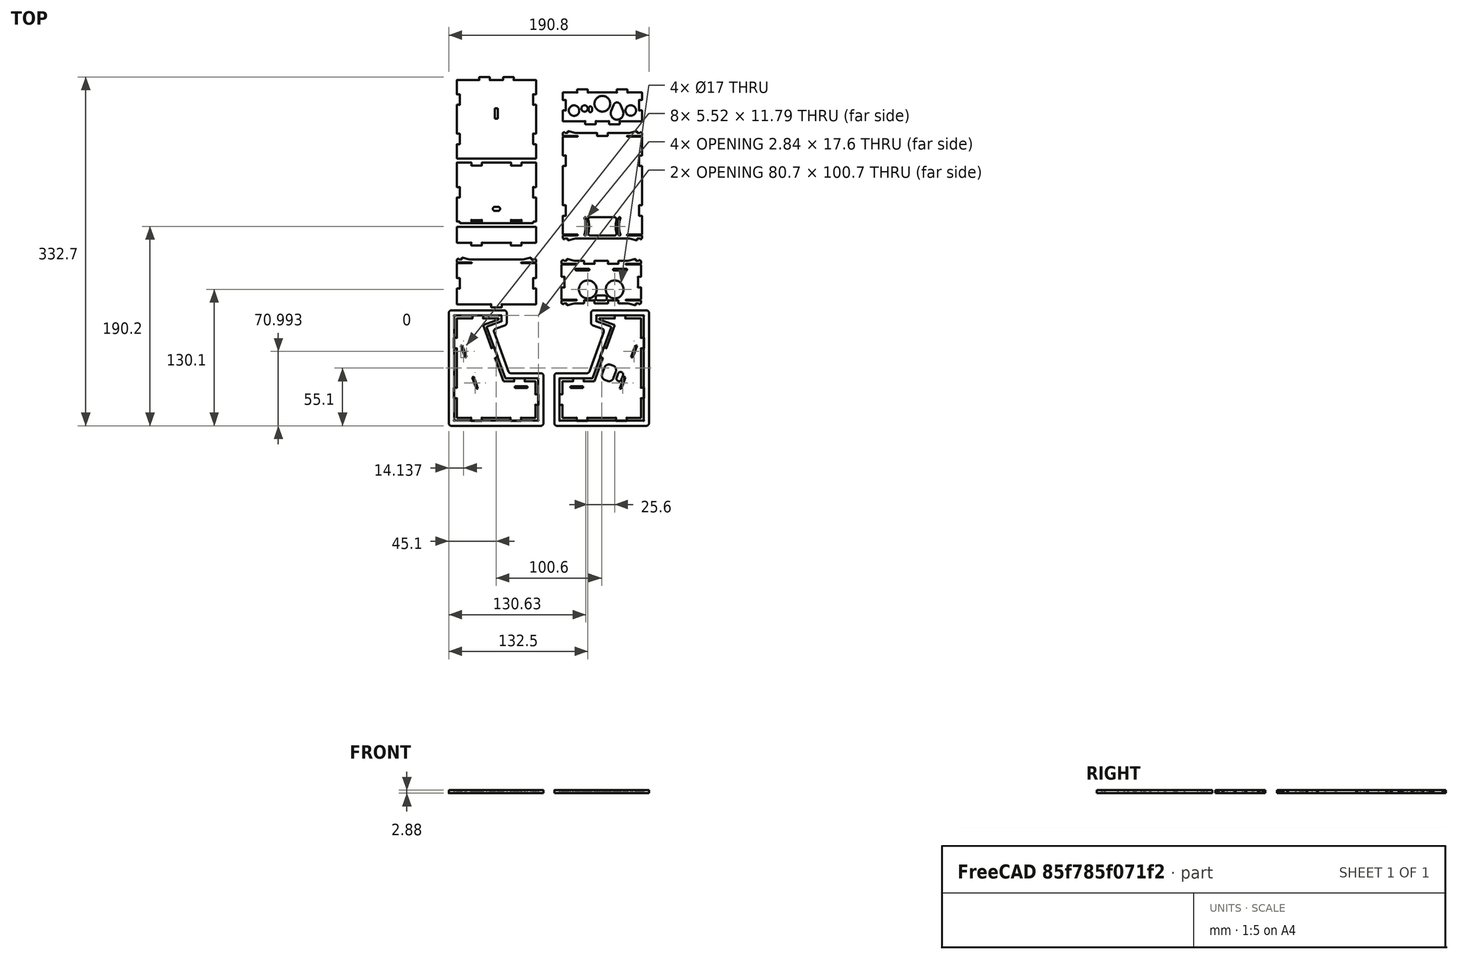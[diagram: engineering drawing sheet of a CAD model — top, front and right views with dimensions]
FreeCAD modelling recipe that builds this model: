
FCSTD DOCUMENT  (FreeCAD 1.0R39319 (Git))
Label: TheThing_v81_tabs_export
License: CERN Open Hardware Licence permissive
LicenseURL: https://cern-ohl.web.cern.ch/
objects: Part::Part2DObjectPython×13, Part::Feature×11, App::FeaturePython×11, Sketcher::SketchObject×10, Part::Chamfer×9, App::DocumentObjectGroup×4
note: 53 computed .brp shape members not serialized (recipe doc carries the construction recipe); baked Part::Feature solids carry a one-line shape summary decoded from their .brp

FEATURE [Part::Feature] test
  Placement = pos=(171.5,47,-35) rot=(-0.57735,-0.57735,-0.57735;2.0944rad)
  shape: bbox 80.6 x 100.6 x 2.8 mm, 82 faces (baked)
FEATURE [Part::Feature] test001
  Placement = pos=(30.5,47,-35) rot=(0.57735,-0.57735,-0.57735;4.18879rad)
  shape: bbox 80.6 x 100.6 x 2.8 mm, 70 faces (baked)
FEATURE [Part::Feature] test002
  Placement = pos=(152,221,20.1) rot=(-1,0,0;1.5708rad)
  shape: bbox 75.6 x 104.6 x 2.8 mm, 104 faces (baked)
FEATURE [Part::Feature] test003
  Placement = pos=(51,208,-25.7) rot=(-0.939693,0,0;1.22173rad)
  shape: bbox 75.6 x 58.11 x 2.925 mm, 56 faces (baked)
FEATURE [Part::Feature] test004
  Placement = pos=(152,353,-0.4) rot=(0,0,1;0rad)
  shape: bbox 75.6 x 33.14 x 2.8 mm, 54 faces (baked)
FEATURE [Part::Feature] test005
  Placement = pos=(150.9,159,60.5) rot=(0,0.707107,0.707107;3.14159rad)
  shape: bbox 75.6 x 44.6 x 2.8 mm, 108 faces (baked)
FEATURE [Part::Feature] test006
  Placement = pos=(51,277,-34.6) rot=(1,0,0;3.14159rad)
  shape: bbox 75.6 x 77.8 x 2.8 mm, 46 faces (baked)
FEATURE [Part::Feature] test007
  Placement = pos=(51,138,-60.4) rot=(0,0,1;3.14159rad)
  shape: bbox 75.6 x 47.6 x 2.8 mm, 50 faces (baked)
FEATURE [Part::Feature] test008
  Placement = pos=(51,151,48.1) rot=(-0.34202,0,0;2.79253rad)
  shape: bbox 75.6 x 17.92 x 2.8 mm, 18 faces (baked)
FEATURE [Part::Feature] test009
  Placement = pos=(171.5,47,-33) rot=(-0.57735,-0.57735,-0.57735;2.0944rad)
  shape: bbox 90.2 x 110.2 x 2.8 mm, 46 faces (baked)
FEATURE [Part::Feature] test010
  Placement = pos=(30.5,47,-33) rot=(0.57735,-0.57735,-0.57735;4.18879rad)
  shape: bbox 90.2 x 110.2 x 2.8 mm, 46 faces (baked)
FEATURE [Sketcher::SketchObject] Sketch
  ArcFitTolerance = 1e-06
  FullyConstrained = true
  MakeInternals = false
  sketch-geometry (52):
    g0: LineSegment StartX=5 StartY=0 StartZ=0 EndX=95 EndY=0 EndZ=0
    g1: LineSegment StartX=100 StartY=5 StartZ=0 EndX=100 EndY=165 EndZ=0
    g2: LineSegment StartX=95 StartY=170 StartZ=0 EndX=5 EndY=170 EndZ=0
    g3: LineSegment StartX=0 StartY=165 StartZ=0 EndX=0 EndY=5 EndZ=0
    g4: LineSegment StartX=5 StartY=171 StartZ=0 EndX=95 EndY=171 EndZ=0
    g5: LineSegment StartX=100 StartY=176 StartZ=0 EndX=100 EndY=336 EndZ=0
    g6: LineSegment StartX=95 StartY=341 StartZ=0 EndX=5 EndY=341 EndZ=0
    g7: LineSegment StartX=0 StartY=336 StartZ=0 EndX=0 EndY=176 EndZ=0
    g8: LineSegment StartX=106 StartY=171 StartZ=0 EndX=196 EndY=171 EndZ=0
    g9: LineSegment StartX=201 StartY=176 StartZ=0 EndX=201 EndY=336 EndZ=0
    g10: LineSegment StartX=196 StartY=341 StartZ=0 EndX=106 EndY=341 EndZ=0
    g11: LineSegment StartX=101 StartY=336 StartZ=0 EndX=101 EndY=176 EndZ=0
    g12: LineSegment StartX=106 StartY=0 StartZ=0 EndX=196 EndY=0 EndZ=0
    g13: LineSegment StartX=201 StartY=5 StartZ=0 EndX=201 EndY=165 EndZ=0
    g14: LineSegment StartX=196 StartY=170 StartZ=0 EndX=106 EndY=170 EndZ=0
    g15: LineSegment StartX=101 StartY=165 StartZ=0 EndX=101 EndY=5 EndZ=0
    g16: LineSegment [constr] StartX=100 StartY=170 StartZ=0 EndX=101 EndY=170 EndZ=0
    g17: LineSegment [constr] StartX=101 StartY=170 StartZ=0 EndX=101 EndY=171 EndZ=0
    g18: LineSegment [constr] StartX=101 StartY=171 StartZ=0 EndX=100 EndY=171 EndZ=0
    g19: LineSegment [constr] StartX=100 StartY=171 StartZ=0 EndX=100 EndY=170 EndZ=0
    g20: ArcOfCircle CenterX=5 CenterY=5 CenterZ=0 NormalX=0 NormalY=0 NormalZ=1 AngleXU=0 Radius=5 StartAngle=3.14159 EndAngle=4.71239
    g21: GeomPoint [constr] X=0 Y=0 Z=0
    g22: ArcOfCircle CenterX=95 CenterY=5 CenterZ=0 NormalX=0 NormalY=0 NormalZ=1 AngleXU=0 Radius=5 StartAngle=4.71239 EndAngle=6.28319
    g23: GeomPoint [constr] X=100 Y=0 Z=0
    g24: ArcOfCircle CenterX=106 CenterY=5 CenterZ=0 NormalX=0 NormalY=0 NormalZ=1 AngleXU=0 Radius=5 StartAngle=3.14159 EndAngle=4.71239
    g25: GeomPoint [constr] X=101 Y=0 Z=0
    g26: ArcOfCircle CenterX=196 CenterY=5 CenterZ=0 NormalX=0 NormalY=0 NormalZ=1 AngleXU=0 Radius=5 StartAngle=4.71239 EndAngle=6.28319
    g27: GeomPoint [constr] X=201 Y=0 Z=0
    g28: ArcOfCircle CenterX=95 CenterY=176 CenterZ=0 NormalX=0 NormalY=0 NormalZ=1 AngleXU=0 Radius=5 StartAngle=4.71239 EndAngle=6.28319
    g29: GeomPoint [constr] X=100 Y=171 Z=0
    g30: ArcOfCircle CenterX=95 CenterY=165 CenterZ=0 NormalX=0 NormalY=0 NormalZ=1 AngleXU=0 Radius=5 StartAngle=3e-16 EndAngle=1.5708
    g31: GeomPoint [constr] X=100 Y=170 Z=0
    g32: ArcOfCircle CenterX=106 CenterY=165 CenterZ=0 NormalX=0 NormalY=0 NormalZ=1 AngleXU=0 Radius=5 StartAngle=1.5708 EndAngle=3.14159
    g33: GeomPoint [constr] X=101 Y=170 Z=0
    g34: ArcOfCircle CenterX=106 CenterY=176 CenterZ=0 NormalX=0 NormalY=0 NormalZ=1 AngleXU=0 Radius=5 StartAngle=3.14159 EndAngle=4.71239
    g35: GeomPoint [constr] X=101 Y=171 Z=0
    g36: ArcOfCircle CenterX=5 CenterY=176 CenterZ=0 NormalX=0 NormalY=0 NormalZ=1 AngleXU=0 Radius=5 StartAngle=3.14159 EndAngle=4.71239
    g37: GeomPoint [constr] X=0 Y=171 Z=0
    g38: ArcOfCircle CenterX=196 CenterY=176 CenterZ=0 NormalX=0 NormalY=0 NormalZ=1 AngleXU=0 Radius=5 StartAngle=4.71239 EndAngle=6.28319
    g39: GeomPoint [constr] X=201 Y=171 Z=0
    g40: ArcOfCircle CenterX=196 CenterY=165 CenterZ=0 NormalX=0 NormalY=0 NormalZ=1 AngleXU=0 Radius=5 StartAngle=2.4e-15 EndAngle=1.5708
    g41: GeomPoint [constr] X=201 Y=170 Z=0
    g42: ArcOfCircle CenterX=5 CenterY=165 CenterZ=0 NormalX=0 NormalY=0 NormalZ=1 AngleXU=0 Radius=5 StartAngle=1.5708 EndAngle=3.14159
    g43: GeomPoint [constr] X=0 Y=170 Z=0
    g44: ArcOfCircle CenterX=5 CenterY=336 CenterZ=0 NormalX=0 NormalY=0 NormalZ=1 AngleXU=0 Radius=5 StartAngle=1.5708 EndAngle=3.14159
    g45: GeomPoint [constr] X=0 Y=341 Z=0
    g46: ArcOfCircle CenterX=95 CenterY=336 CenterZ=0 NormalX=0 NormalY=0 NormalZ=1 AngleXU=0 Radius=5 StartAngle=1.7e-15 EndAngle=1.5708
    g47: GeomPoint [constr] X=100 Y=341 Z=0
    g48: ArcOfCircle CenterX=106 CenterY=336 CenterZ=0 NormalX=0 NormalY=0 NormalZ=1 AngleXU=0 Radius=5 StartAngle=1.5708 EndAngle=3.14159
    g49: GeomPoint [constr] X=101 Y=341 Z=0
    g50: ArcOfCircle CenterX=196 CenterY=336 CenterZ=0 NormalX=0 NormalY=0 NormalZ=1 AngleXU=0 Radius=5 StartAngle=-2.7e-15 EndAngle=1.5708
    g51: GeomPoint [constr] X=201 Y=341 Z=0
  constraints (119):
    c: Horizontal(g0)
    c: Horizontal(g2)
    c: Vertical(g1)
    c: Vertical(g3)
    c: Coincident(g21,g-1)
    c: Horizontal(g4)
    c: Horizontal(g6)
    c: Vertical(g5)
    c: Vertical(g7)
    c: Horizontal(g8)
    c: Horizontal(g10)
    c: Vertical(g9)
    c: Vertical(g11)
    c: Horizontal(g12)
    c: Horizontal(g14)
    c: Vertical(g13)
    c: Vertical(g15)
    c: DistanceX(g21,g23) = 100
    c: DistanceY(g21,g43) = 170
    c: Coincident(g16,g17)
    c: Coincident(g17,g18)
    c: Coincident(g18,g19)
    c: Coincident(g19,g16)
    c: Horizontal(g16)
    c: Horizontal(g18)
    c: Vertical(g17)
    c: Vertical(g19)
    c: Distance(g17,g19) = 1
    c: Distance(g16,g18) = 1
    c: Coincident(g16,g31)
    c: Coincident(g18,g29)
    c: Coincident(g17,g35)
    c: Coincident(g16,g33)
    c: PointOnObject(g21,g0)
    c: PointOnObject(g21,g3)
    c: Tangent(g0,g20) = -1.5708
    c: Tangent(g3,g20) = -1.5708
    c: PointOnObject(g23,g0)
    c: PointOnObject(g23,g1)
    c: Tangent(g0,g22) = -1.5708
    c: Tangent(g1,g22) = -1.5708
    c: PointOnObject(g25,g12)
    c: PointOnObject(g25,g15)
    c: Tangent(g12,g24) = -1.5708
    c: Tangent(g15,g24) = -1.5708
    c: PointOnObject(g27,g13)
    c: PointOnObject(g27,g12)
    c: Tangent(g13,g26) = -1.5708
    c: Tangent(g12,g26) = -1.5708
    c: PointOnObject(g29,g5)
    c: PointOnObject(g29,g4)
    c: Tangent(g5,g28) = -1.5708
    c: Tangent(g4,g28) = -1.5708
    c: PointOnObject(g31,g2)
    c: PointOnObject(g31,g1)
    c: Tangent(g2,g30) = -1.5708
    c: Tangent(g1,g30) = -1.5708
    c: PointOnObject(g33,g14)
    c: PointOnObject(g33,g15)
    c: Tangent(g14,g32) = -1.5708
    c: Tangent(g15,g32) = -1.5708
    c: PointOnObject(g35,g8)
    c: PointOnObject(g35,g11)
    c: Tangent(g8,g34) = -1.5708
    c: Tangent(g11,g34) = -1.5708
    c: PointOnObject(g37,g4)
    c: PointOnObject(g37,g7)
    c: Tangent(g4,g36) = -1.5708
    c: Tangent(g7,g36) = -1.5708
    c: PointOnObject(g39,g8)
    c: PointOnObject(g39,g9)
    c: Tangent(g8,g38) = -1.5708
    c: Tangent(g9,g38) = -1.5708
    c: PointOnObject(g41,g14)
    c: PointOnObject(g41,g13)
    c: Tangent(g14,g40) = -1.5708
    c: Tangent(g13,g40) = -1.5708
    c: PointOnObject(g43,g2)
    c: PointOnObject(g43,g3)
    c: Tangent(g2,g42) = -1.5708
    c: Tangent(g3,g42) = -1.5708
    c: PointOnObject(g45,g6)
    c: PointOnObject(g45,g7)
    c: Tangent(g6,g44) = -1.5708
    c: Tangent(g7,g44) = -1.5708
    c: PointOnObject(g47,g6)
    c: PointOnObject(g47,g5)
    c: Tangent(g6,g46) = -1.5708
    c: Tangent(g5,g46) = -1.5708
    c: PointOnObject(g49,g10)
    c: PointOnObject(g49,g11)
    c: Tangent(g10,g48) = -1.5708
    c: Tangent(g11,g48) = -1.5708
    c: PointOnObject(g51,g10)
    c: PointOnObject(g51,g9)
    c: Tangent(g10,g50) = -1.5708
    c: Tangent(g9,g50) = -1.5708
    c: Equal(g50,g48)
    c: Equal(g48,g46)
    c: Equal(g46,g44)
    c: Equal(g44,g36)
    c: Equal(g36,g42)
    c: Equal(g42,g28)
    c: Equal(g28,g34)
    c: Equal(g34,g32)
    c: Equal(g32,g30)
    c: Equal(g30,g38)
    c: Equal(g38,g40)
    c: Equal(g40,g26)
    c: Equal(g26,g24)
    c: Equal(g24,g22)
    c: Equal(g22,g20)
    c: Radius(g20) = 5
    c: Vertical(g37,g43)
    c: Horizontal(g25,g23)
    c: Vertical(g39,g41)
    c: Horizontal(g47,g49)
    c: Equal(g7,g3)
    c: Equal(g6,g10)
FEATURE [Part::Chamfer] Chamfer
  Base = -> test
  EdgeLinks = -> test [Edge25,Edge27,Edge39,Edge50,Edge52,Edge72,Edge74,Edge86,Edge97,Edge99,Edge119,Edge121,Edge133,Edge144,Edge146,Edge158,Edge169,Edge171,Edge194,Edge196]
  Edges = 20 edges r=0.5: [Edge25,Edge27,Edge39,Edge50,Edge52,Edge72,Edge74,Edge86,Edge97,Edge99,Edge119,Edge121,Edge133,Edge144,Edge146,Edge158,Edge169,Edge171,Edge194,Edge196]
FEATURE [Part::Chamfer] Chamfer001
  Base = -> test001
  EdgeLinks = -> test001 [Edge25,Edge27,Edge39,Edge50,Edge52,Edge72,Edge74,Edge86,Edge97,Edge99,Edge119,Edge121,Edge133,Edge144,Edge146,Edge158,Edge169,Edge171,Edge194,Edge196]
  Edges = 20 edges r=0.5: [Edge25,Edge27,Edge39,Edge50,Edge52,Edge72,Edge74,Edge86,Edge97,Edge99,Edge119,Edge121,Edge133,Edge144,Edge146,Edge158,Edge169,Edge171,Edge194,Edge196]
FEATURE [Part::Chamfer] Chamfer002
  Base = -> test002
  EdgeLinks = -> test002 [Edge227,Edge232,Edge233,Edge238,Edge267,Edge272,Edge273,Edge278,Edge293,Edge298]
  Edges = 10 edges r=0.5: [Edge227,Edge232,Edge233,Edge238,Edge267,Edge272,Edge273,Edge278,Edge293,Edge298]
FEATURE [Part::Chamfer] Chamfer003
  Base = -> test003
  EdgeLinks = -> test003 [Edge2,Edge4,Edge104,Edge105,Edge107,Edge118,Edge142,Edge143,Edge148,Edge149,Edge150,Edge155,Edge156,Edge164]
  Edges = 14 edges r=0.5: [Edge2,Edge4,Edge104,Edge105,Edge107,Edge118,Edge142,Edge143,Edge148,Edge149,Edge150,Edge155,Edge156,Edge164]
FEATURE [Part::Chamfer] Chamfer004
  Base = -> test004
  EdgeLinks = -> test004 [Edge4,Edge7,Edge17,Edge20,Edge39,Edge42,Edge52,Edge55,Edge69,Edge73,Edge85,Edge88,Edge107,Edge110,Edge115,Edge123]
  Edges = 16 edges: [Edge4 r=0.5,Edge7 r=1,Edge17 r=0.5,Edge20 r=0.5,Edge39 r=0.5,Edge42 r=0.5,Edge52 r=0.5,Edge55 r=0.5,Edge69 r=0.5,Edge73 r=0.5,Edge85 r=0.5,Edge88 r=0.5,Edge107 r=0.5,Edge110 r=0.5,Edge115 r=0.5,Edge123 r=0.5]
FEATURE [Part::Chamfer] Chamfer005
  Base = -> test005
  EdgeLinks = -> test005 [Edge243,Edge248,Edge249,Edge254,Edge269,Edge274,Edge289,Edge294,Edge295,Edge300,Edge315,Edge320]
  Edges = 12 edges r=0.5: [Edge243,Edge248,Edge249,Edge254,Edge269,Edge274,Edge289,Edge294,Edge295,Edge300,Edge315,Edge320]
FEATURE [Part::Chamfer] Chamfer006
  Base = -> test006
  EdgeLinks = -> test006 [Edge1,Edge2,Edge7,Edge9,Edge27,Edge30,Edge45,Edge48,Edge59,Edge61,Edge81,Edge83,Edge95,Edge98,Edge125,Edge126]
  Edges = 16 edges r=0.5: [Edge1,Edge2,Edge7,Edge9,Edge27,Edge30,Edge45,Edge48,Edge59,Edge61,Edge81,Edge83,Edge95,Edge98,Edge125,Edge126]
FEATURE [Part::Chamfer] Chamfer007
  Base = -> test007
  EdgeLinks = -> test007 [Edge4,Edge6,Edge17,Edge20,Edge87,Edge103,Edge106,Edge120]
  Edges = 8 edges r=0.5: [Edge4,Edge6,Edge17,Edge20,Edge87,Edge103,Edge106,Edge120]
FEATURE [Part::Chamfer] Chamfer008
  Base = -> test008
  EdgeLinks = -> test008 [Edge1,Edge2,Edge5,Edge8,Edge28,Edge31,Edge50,Edge53]
  Edges = 8 edges r=0.5: [Edge1,Edge2,Edge5,Edge8,Edge28,Edge31,Edge50,Edge53]
FEATURE [Part::Part2DObjectPython] Shape2DView  # Draft 2D object (typed FeaturePython)
  AutoUpdate = true
  Clip = false
  FuseArch = false
  HiddenLines = false
  InPlace = true
  OnlySolids = false
  Placement = pos=(92,350,3) rot=(0,0,1;1.5708rad)
  Projection = (-0.0061258,0.0189136,0.999802)
  ProjectionMode = 0
  SegmentLength = 0.05
  Tessellation = false
  VisibleOnly = false
FEATURE [Part::Part2DObjectPython] Shape2DView001  # Draft 2D object (typed FeaturePython)
  AutoUpdate = true
  Clip = false
  FuseArch = false
  HiddenLines = false
  InPlace = true
  OnlySolids = false
  Placement = pos=(138,9,3) rot=(0,0,1;3.14159rad)
  Projection = (0,0,1)
  ProjectionMode = 0
  SegmentLength = 0.05
  Tessellation = false
  VisibleOnly = false
FEATURE [App::FeaturePython] Text  # WARN: FeaturePython — macro-defined, semantics opaque (R4)
  Placement = pos=(167,104,0) rot=(0,0,1;0rad)
  Text = [1]
FEATURE [App::FeaturePython] Text001  # WARN: FeaturePython — macro-defined, semantics opaque (R4)
  Placement = pos=(31,104,0) rot=(0,0,1;0rad)
  Text = [2]
FEATURE [App::FeaturePython] Text002  # WARN: FeaturePython — macro-defined, semantics opaque (R4)
  Placement = pos=(150,277,0) rot=(0,0,1;0rad)
  Text = [3]
FEATURE [App::FeaturePython] Text003  # WARN: FeaturePython — macro-defined, semantics opaque (R4)
  Placement = pos=(49,249,0) rot=(0,0,1;0rad)
  Text = [4]
FEATURE [App::FeaturePython] Text004  # WARN: FeaturePython — macro-defined, semantics opaque (R4)
  Placement = pos=(150,320,0) rot=(0,0,1;0rad)
  Text = [5]
FEATURE [App::FeaturePython] Text005  # WARN: FeaturePython — macro-defined, semantics opaque (R4)
  Placement = pos=(149,156,0) rot=(0,0,1;0rad)
  Text = [6]
FEATURE [App::FeaturePython] Text006  # WARN: FeaturePython — macro-defined, semantics opaque (R4)
  Placement = pos=(49,331,0) rot=(0,0,1;0rad)
  Text = [7]
FEATURE [App::FeaturePython] Text007  # WARN: FeaturePython — macro-defined, semantics opaque (R4)
  Placement = pos=(48,160,0) rot=(0,0,1;0rad)
  Text = [8]
FEATURE [App::FeaturePython] Text008  # WARN: FeaturePython — macro-defined, semantics opaque (R4)
  Placement = pos=(49,191,0) rot=(0,0,1;0rad)
  Text = [9]
FEATURE [App::FeaturePython] Text009  # WARN: FeaturePython — macro-defined, semantics opaque (R4)
  Placement = pos=(166,111.5,0) rot=(0,0,1;0rad)
  Text = [10]
FEATURE [App::FeaturePython] Text010  # WARN: FeaturePython — macro-defined, semantics opaque (R4)
  Placement = pos=(30,111.5,0) rot=(0,0,1;0rad)
  Text = [11]
FEATURE [App::DocumentObjectGroup] Group  label="Numbers"
  Group = -> [Text,Text001,Text002,Text003,Text004,Text005,Text006,Text007,Text008,Text009,Text010]
FEATURE [App::DocumentObjectGroup] Group001  label="Logos"
  Group = -> [Shape2DView,Shape2DView001]
FEATURE [Part::Part2DObjectPython] Shape2DView002  # Draft 2D object (typed FeaturePython)
  AutoUpdate = true
  Base = -> test009
  Clip = false
  FuseArch = false
  HiddenLines = false
  InPlace = true
  OnlySolids = false
  Projection = (0,0,1)
  ProjectionMode = 0
  SegmentLength = 0.05
  Tessellation = false
  VisibleOnly = false
FEATURE [Part::Part2DObjectPython] Shape2DView003  # Draft 2D object (typed FeaturePython)
  AutoUpdate = true
  Base = -> Chamfer
  Clip = false
  FuseArch = false
  HiddenLines = false
  InPlace = true
  OnlySolids = false
  Projection = (0,0,1)
  ProjectionMode = 0
  SegmentLength = 0.05
  Tessellation = false
  VisibleOnly = false
FEATURE [Part::Part2DObjectPython] Shape2DView004  # Draft 2D object (typed FeaturePython)
  AutoUpdate = true
  Base = -> test010
  Clip = false
  FuseArch = false
  HiddenLines = false
  InPlace = true
  OnlySolids = false
  Projection = (0,0,1)
  ProjectionMode = 0
  SegmentLength = 0.05
  Tessellation = false
  VisibleOnly = false
FEATURE [Part::Part2DObjectPython] Shape2DView005  # Draft 2D object (typed FeaturePython)
  AutoUpdate = true
  Base = -> Chamfer001
  Clip = false
  FuseArch = false
  HiddenLines = false
  InPlace = true
  OnlySolids = false
  Projection = (0,0,1)
  ProjectionMode = 0
  SegmentLength = 0.05
  Tessellation = false
  VisibleOnly = false
FEATURE [Part::Part2DObjectPython] Shape2DView006  # Draft 2D object (typed FeaturePython)
  AutoUpdate = true
  Base = -> Chamfer002
  Clip = false
  FuseArch = false
  HiddenLines = false
  InPlace = true
  OnlySolids = false
  Projection = (0,0,1)
  ProjectionMode = 0
  SegmentLength = 0.05
  Tessellation = false
  VisibleOnly = false
FEATURE [Part::Part2DObjectPython] Shape2DView007  # Draft 2D object (typed FeaturePython)
  AutoUpdate = true
  Base = -> Chamfer003
  Clip = false
  FuseArch = false
  HiddenLines = false
  InPlace = true
  OnlySolids = false
  Projection = (0,0,1)
  ProjectionMode = 0
  SegmentLength = 0.05
  Tessellation = false
  VisibleOnly = false
FEATURE [Part::Part2DObjectPython] Shape2DView008  # Draft 2D object (typed FeaturePython)
  AutoUpdate = true
  Base = -> Chamfer004
  Clip = false
  FuseArch = false
  HiddenLines = false
  InPlace = true
  OnlySolids = false
  Projection = (0,0,1)
  ProjectionMode = 0
  SegmentLength = 0.05
  Tessellation = false
  VisibleOnly = false
FEATURE [Part::Part2DObjectPython] Shape2DView009  # Draft 2D object (typed FeaturePython)
  AutoUpdate = true
  Base = -> Chamfer005
  Clip = false
  FuseArch = false
  HiddenLines = false
  InPlace = true
  OnlySolids = false
  Projection = (0,0,1)
  ProjectionMode = 0
  SegmentLength = 0.05
  Tessellation = false
  VisibleOnly = false
FEATURE [Part::Part2DObjectPython] Shape2DView010  # Draft 2D object (typed FeaturePython)
  AutoUpdate = true
  Base = -> Chamfer006
  Clip = false
  FuseArch = false
  HiddenLines = false
  InPlace = true
  OnlySolids = false
  Projection = (0,0,1)
  ProjectionMode = 0
  SegmentLength = 0.05
  Tessellation = false
  VisibleOnly = false
FEATURE [Part::Part2DObjectPython] Shape2DView011  # Draft 2D object (typed FeaturePython)
  AutoUpdate = true
  Base = -> Chamfer007
  Clip = false
  FuseArch = false
  HiddenLines = false
  InPlace = true
  OnlySolids = false
  Projection = (0,0,1)
  ProjectionMode = 0
  SegmentLength = 0.05
  Tessellation = false
  VisibleOnly = false
FEATURE [Part::Part2DObjectPython] Shape2DView012  # Draft 2D object (typed FeaturePython)
  AutoUpdate = true
  Base = -> Chamfer008
  Clip = false
  FuseArch = false
  HiddenLines = false
  InPlace = true
  OnlySolids = false
  Projection = (0,0,1)
  ProjectionMode = 0
  SegmentLength = 0.05
  Tessellation = false
  VisibleOnly = false
FEATURE [Sketcher::SketchObject] Sketch001
  ArcFitTolerance = 1e-06
  FullyConstrained = false
  MakeInternals = false
  sketch-geometry (152):
    g0: LineSegment StartX=143.7 StartY=115 StartZ=0 EndX=193.9 EndY=115 EndZ=0
    g1: ArcOfCircle CenterX=143.7 CenterY=112.5 CenterZ=0 NormalX=0 NormalY=0 NormalZ=1 AngleXU=1.8e-15 Radius=2.5 StartAngle=1.5708 EndAngle=3.14159
    g2: ArcOfCircle CenterX=193.9 CenterY=112.5 CenterZ=0 NormalX=0 NormalY=0 NormalZ=1 AngleXU=1.8e-15 Radius=2.5 StartAngle=0 EndAngle=1.5708
    g3: LineSegment StartX=141.2 StartY=103.131 StartZ=0 EndX=141.2 EndY=112.5 EndZ=0
    g4: LineSegment StartX=196.4 StartY=112.5 StartZ=0 EndX=196.4 EndY=7.3 EndZ=0
    g5: ArcOfCircle CenterX=143.7 CenterY=103.131 CenterZ=0 NormalX=0 NormalY=0 NormalZ=1 AngleXU=1.8e-15 Radius=2.5 StartAngle=3.14159 EndAngle=4.36332
    g6: ArcOfCircle CenterX=193.9 CenterY=7.3 CenterZ=0 NormalX=0 NormalY=0 NormalZ=1 AngleXU=1.8e-15 Radius=2.5 StartAngle=4.71239 EndAngle=6.28319
    g7: LineSegment StartX=151.813 StartY=97.5174 StartZ=0 EndX=142.845 EndY=100.781 EndZ=0
    g8: LineSegment StartX=193.9 StartY=4.8 StartZ=0 EndX=108.7 EndY=4.8 EndZ=0
    g9: ArcOfCircle CenterX=150.958 CenterY=95.1682 CenterZ=0 NormalX=0 NormalY=0 NormalZ=1 AngleXU=1.8e-15 Radius=2.5 StartAngle=5.93412 EndAngle=7.50492
    g10: ArcOfCircle CenterX=108.7 CenterY=7.3 CenterZ=0 NormalX=0 NormalY=0 NormalZ=1 AngleXU=1.8e-15 Radius=2.5 StartAngle=3.14159 EndAngle=4.71239
    g11: LineSegment StartX=139.597 StartY=56.6449 StartZ=0 EndX=153.307 EndY=94.3131 EndZ=0
    g12: LineSegment StartX=106.2 StartY=7.3 StartZ=0 EndX=106.2 EndY=52.5 EndZ=0
    g13: ArcOfCircle CenterX=137.248 CenterY=57.5 CenterZ=0 NormalX=0 NormalY=0 NormalZ=1 AngleXU=1.8e-15 Radius=2.5 StartAngle=4.71239 EndAngle=5.93412
    g14: ArcOfCircle CenterX=108.7 CenterY=52.5 CenterZ=0 NormalX=0 NormalY=0 NormalZ=1 AngleXU=1.8e-15 Radius=2.5 StartAngle=1.5708 EndAngle=3.14159
    g15: LineSegment StartX=108.7 StartY=55 StartZ=0 EndX=137.248 EndY=55 EndZ=0
    g16: ArcOfCircle CenterX=146.633 CenterY=110.25 CenterZ=0 NormalX=0 NormalY=0 NormalZ=1 AngleXU=1.7e-15 Radius=0.25 StartAngle=3.66519 EndAngle=4.71239
    g17: ArcOfCircle CenterX=146.2 CenterY=110 CenterZ=0 NormalX=0 NormalY=0 NormalZ=1 AngleXU=1.7e-15 Radius=0.25 StartAngle=0.523599 EndAngle=4.18879
    g18: ArcOfCircle CenterX=145.95 CenterY=109.567 CenterZ=0 NormalX=0 NormalY=0 NormalZ=1 AngleXU=1.7e-15 Radius=0.25 StartAngle=-8.9e-15 EndAngle=1.0472
    g19: LineSegment StartX=146.2 StartY=104.993 StartZ=0 EndX=146.2 EndY=109.567 EndZ=0
    g20: ArcOfCircle CenterX=145.95 CenterY=104.993 CenterZ=0 NormalX=0 NormalY=0 NormalZ=1 AngleXU=1.7e-15 Radius=0.25 StartAngle=5.23599 EndAngle=6.28319
    g21: ArcOfCircle CenterX=146.2 CenterY=104.56 CenterZ=0 NormalX=0 NormalY=0 NormalZ=1 AngleXU=1.7e-15 Radius=0.25 StartAngle=2.0944 EndAngle=5.41052
    g22: ArcOfCircle CenterX=146.521 CenterY=104.177 CenterZ=0 NormalX=0 NormalY=0 NormalZ=1 AngleXU=1.7e-15 Radius=0.25 StartAngle=1.22173 EndAngle=2.26893
    g23: LineSegment StartX=159.528 StartY=99.7094 StartZ=0 EndX=146.607 EndY=104.412 EndZ=0
    g24: ArcOfCircle CenterX=159.186 CenterY=98.7697 CenterZ=0 NormalX=0 NormalY=0 NormalZ=1 AngleXU=1.8e-15 Radius=1 StartAngle=5.93412 EndAngle=7.50492
    g25: LineSegment StartX=142.739 StartY=50.658 StartZ=0 EndX=160.126 EndY=98.4277 EndZ=0
    g26: ArcOfCircle CenterX=141.799 CenterY=51 CenterZ=0 NormalX=0 NormalY=0 NormalZ=1 AngleXU=1.8e-15 Radius=1 StartAngle=4.71239 EndAngle=5.93412
    g27: LineSegment StartX=111.633 StartY=50 StartZ=0 EndX=141.799 EndY=50 EndZ=0
    g28: ArcOfCircle CenterX=111.633 CenterY=50.25 CenterZ=0 NormalX=0 NormalY=0 NormalZ=1 AngleXU=1.7e-15 Radius=0.25 StartAngle=3.66519 EndAngle=4.71239
    g29: ArcOfCircle CenterX=111.2 CenterY=50 CenterZ=0 NormalX=0 NormalY=0 NormalZ=1 AngleXU=1.7e-15 Radius=0.25 StartAngle=0.523599 EndAngle=4.18879
    g30: ArcOfCircle CenterX=110.95 CenterY=49.567 CenterZ=0 NormalX=0 NormalY=0 NormalZ=1 AngleXU=1.7e-15 Radius=0.25 StartAngle=1e-15 EndAngle=1.0472
    g31: LineSegment StartX=111.2 StartY=10.233 StartZ=0 EndX=111.2 EndY=49.567 EndZ=0
    g32: ArcOfCircle CenterX=110.95 CenterY=10.233 CenterZ=0 NormalX=0 NormalY=0 NormalZ=1 AngleXU=1.7e-15 Radius=0.25 StartAngle=5.23599 EndAngle=6.28319
    g33: ArcOfCircle CenterX=111.2 CenterY=9.8 CenterZ=0 NormalX=0 NormalY=0 NormalZ=1 AngleXU=1.7e-15 Radius=0.25 StartAngle=2.0944 EndAngle=5.75959
    g34: ArcOfCircle CenterX=111.633 CenterY=9.55 CenterZ=0 NormalX=0 NormalY=0 NormalZ=1 AngleXU=1.7e-15 Radius=0.25 StartAngle=1.5708 EndAngle=2.61799
    g35: LineSegment StartX=190.967 StartY=9.8 StartZ=0 EndX=111.633 EndY=9.8 EndZ=0
    g36: ArcOfCircle CenterX=190.967 CenterY=9.55 CenterZ=0 NormalX=0 NormalY=0 NormalZ=1 AngleXU=1.7e-15 Radius=0.25 StartAngle=0.523599 EndAngle=1.5708
    g37: ArcOfCircle CenterX=191.4 CenterY=9.8 CenterZ=0 NormalX=0 NormalY=0 NormalZ=1 AngleXU=1.7e-15 Radius=0.25 StartAngle=3.66519 EndAngle=7.33038
    g38: ArcOfCircle CenterX=191.65 CenterY=10.233 CenterZ=0 NormalX=0 NormalY=0 NormalZ=1 AngleXU=1.7e-15 Radius=0.25 StartAngle=3.14159 EndAngle=4.18879
    g39: LineSegment StartX=191.4 StartY=109.567 StartZ=0 EndX=191.4 EndY=10.233 EndZ=0
    g40: ArcOfCircle CenterX=191.65 CenterY=109.567 CenterZ=0 NormalX=0 NormalY=0 NormalZ=1 AngleXU=1.7e-15 Radius=0.25 StartAngle=2.0944 EndAngle=3.14159
    g41: ArcOfCircle CenterX=191.4 CenterY=110 CenterZ=0 NormalX=0 NormalY=0 NormalZ=1 AngleXU=1.7e-15 Radius=0.25 StartAngle=5.23599 EndAngle=8.90118
    g42: ArcOfCircle CenterX=190.967 CenterY=110.25 CenterZ=0 NormalX=0 NormalY=0 NormalZ=1 AngleXU=1.7e-15 Radius=0.25 StartAngle=4.71239 EndAngle=5.75959
    g43: LineSegment StartX=146.633 StartY=110 StartZ=0 EndX=190.967 EndY=110 EndZ=0
    g44: LineSegment StartX=163.725 StartY=107.587 StartZ=0 EndX=163.725 EndY=109.7 EndZ=0
    g45: LineSegment StartX=163.725 StartY=109.7 StartZ=0 EndX=164.025 EndY=110 EndZ=0
    g46: ArcOfCircle CenterX=163.725 CenterY=107.4 CenterZ=0 NormalX=0 NormalY=0 NormalZ=1 AngleXU=1.5708 Radius=0.186667 StartAngle=1.5708 EndAngle=4.71239
    g47: ArcOfCircle CenterX=163.725 CenterY=107.4 CenterZ=0 NormalX=0 NormalY=0 NormalZ=1 AngleXU=1.5708 Radius=0.186667 StartAngle=4.71239 EndAngle=6.28319
    g48: LineSegment StartX=155.62 StartY=78.9934 StartZ=0 EndX=153.634 EndY=79.7163 EndZ=0
    g49: LineSegment StartX=153.25 StartY=79.5369 StartZ=0 EndX=153.634 EndY=79.7163 EndZ=0
    g50: ArcOfCircle CenterX=155.796 CenterY=78.9296 CenterZ=0 NormalX=0 NormalY=0 NormalZ=1 AngleXU=2.79253 Radius=0.186667 StartAngle=0 EndAngle=1.5708
    g51: ArcOfCircle CenterX=155.796 CenterY=78.9296 CenterZ=0 NormalX=0 NormalY=0 NormalZ=1 AngleXU=2.79253 Radius=0.186667 StartAngle=1.5708 EndAngle=4.71239
    g52: LineSegment StartX=150.163 StartY=70.1784 StartZ=0 EndX=149.984 EndY=70.5629 EndZ=0
    g53: LineSegment StartX=155.86 StartY=79.105 StartZ=0 EndX=163.8 EndY=100.921 EndZ=0
    g54: LineSegment StartX=152.149 StartY=69.4556 StartZ=0 EndX=150.163 EndY=70.1784 EndZ=0
    g55: LineSegment StartX=163.8 StartY=100.921 StartZ=0 EndX=148.8 EndY=106.381 EndZ=0
    g56: ArcOfCircle CenterX=152.324 CenterY=69.3917 CenterZ=0 NormalX=0 NormalY=0 NormalZ=1 AngleXU=2.79253 Radius=0.186667 StartAngle=4.71239 EndAngle=6.28319
    g57: LineSegment StartX=148.8 StartY=106.381 StartZ=0 EndX=148.8 EndY=107.4 EndZ=0
    g58: ArcOfCircle CenterX=152.324 CenterY=69.3917 CenterZ=0 NormalX=0 NormalY=0 NormalZ=1 AngleXU=2.79253 Radius=0.186667 StartAngle=1.5708 EndAngle=4.71239
    g59: LineSegment StartX=148.8 StartY=107.4 StartZ=0 EndX=163.538 EndY=107.4 EndZ=0
    g60: LineSegment StartX=144.32 StartY=47.4 StartZ=0 EndX=152.26 EndY=69.2163 EndZ=0
    g61: LineSegment StartX=134.322 StartY=47.4 StartZ=0 EndX=144.32 EndY=47.4 EndZ=0
    g62: ArcOfCircle CenterX=134.135 CenterY=47.4 CenterZ=0 NormalX=0 NormalY=0 NormalZ=1 AngleXU=1.5708 Radius=0.186667 StartAngle=1.5708 EndAngle=4.71239
    g63: ArcOfCircle CenterX=134.135 CenterY=47.4 CenterZ=0 NormalX=0 NormalY=0 NormalZ=1 AngleXU=1.5708 Radius=0.186667 StartAngle=0 EndAngle=1.5708
    g64: LineSegment StartX=134.135 StartY=47.5867 StartZ=0 EndX=134.135 EndY=49.7 EndZ=0
    g65: LineSegment StartX=133.835 StartY=50 StartZ=0 EndX=134.135 EndY=49.7 EndZ=0
    g66: LineSegment StartX=173.575 StartY=110 StartZ=0 EndX=173.875 EndY=109.7 EndZ=0
    g67: LineSegment StartX=173.875 StartY=107.587 StartZ=0 EndX=173.875 EndY=109.7 EndZ=0
    g68: LineSegment StartX=123.985 StartY=49.7 StartZ=0 EndX=124.285 EndY=50 EndZ=0
    g69: ArcOfCircle CenterX=173.875 CenterY=107.4 CenterZ=0 NormalX=0 NormalY=0 NormalZ=1 AngleXU=1.5708 Radius=0.186667 StartAngle=0 EndAngle=1.5708
    g70: LineSegment StartX=123.985 StartY=47.5867 StartZ=0 EndX=123.985 EndY=49.7 EndZ=0
    g71: ArcOfCircle CenterX=173.875 CenterY=107.4 CenterZ=0 NormalX=0 NormalY=0 NormalZ=1 AngleXU=1.5708 Radius=0.186667 StartAngle=1.5708 EndAngle=4.71239
    g72: ArcOfCircle CenterX=123.985 CenterY=47.4 CenterZ=0 NormalX=0 NormalY=0 NormalZ=1 AngleXU=1.5708 Radius=0.186667 StartAngle=4.71239 EndAngle=6.28319
    g73: LineSegment StartX=174.062 StartY=107.4 StartZ=0 EndX=188.3 EndY=107.4 EndZ=0
    g74: ArcOfCircle CenterX=123.985 CenterY=47.4 CenterZ=0 NormalX=0 NormalY=0 NormalZ=1 AngleXU=1.5708 Radius=0.186667 StartAngle=1.5708 EndAngle=4.71239
    g75: LineSegment StartX=188.3 StartY=107.4 StartZ=0 EndX=188.8 EndY=106.9 EndZ=0
    g76: LineSegment StartX=114.3 StartY=47.4 StartZ=0 EndX=123.798 EndY=47.4 EndZ=0
    g77: LineSegment StartX=188.8 StartY=106.9 StartZ=0 EndX=188.8 EndY=88.9117 EndZ=0
    g78: LineSegment StartX=113.8 StartY=46.9 StartZ=0 EndX=114.3 EndY=47.4 EndZ=0
    g79: ArcOfCircle CenterX=188.8 CenterY=88.725 CenterZ=0 NormalX=0 NormalY=0 NormalZ=1 AngleXU=2e-16 Radius=0.186667 StartAngle=1.5708 EndAngle=4.71239
    g80: LineSegment StartX=113.8 StartY=35.1617 StartZ=0 EndX=113.8 EndY=46.9 EndZ=0
    g81: ArcOfCircle CenterX=188.8 CenterY=88.725 CenterZ=0 NormalX=0 NormalY=0 NormalZ=1 AngleXU=2e-16 Radius=0.186667 StartAngle=4.71239 EndAngle=6.28319
    g82: ArcOfCircle CenterX=113.8 CenterY=34.975 CenterZ=0 NormalX=0 NormalY=0 NormalZ=1 AngleXU=-3.14159 Radius=0.186667 StartAngle=1.5708 EndAngle=4.71239
    g83: LineSegment StartX=188.987 StartY=88.725 StartZ=0 EndX=191.1 EndY=88.725 EndZ=0
    g84: ArcOfCircle CenterX=113.8 CenterY=34.975 CenterZ=0 NormalX=0 NormalY=0 NormalZ=1 AngleXU=-3.14159 Radius=0.186667 StartAngle=0 EndAngle=1.5708
    g85: LineSegment StartX=191.1 StartY=88.725 StartZ=0 EndX=191.4 EndY=88.425 EndZ=0
    g86: LineSegment StartX=113.613 StartY=34.975 StartZ=0 EndX=111.5 EndY=34.975 EndZ=0
    g87: LineSegment StartX=111.2 StartY=34.675 StartZ=0 EndX=111.5 EndY=34.975 EndZ=0
    g88: LineSegment StartX=191.4 StartY=78.875 StartZ=0 EndX=191.1 EndY=78.575 EndZ=0
    g89: LineSegment StartX=188.987 StartY=78.575 StartZ=0 EndX=191.1 EndY=78.575 EndZ=0
    g90: LineSegment StartX=111.5 StartY=24.825 StartZ=0 EndX=111.2 EndY=25.125 EndZ=0
    g91: ArcOfCircle CenterX=188.8 CenterY=78.575 CenterZ=0 NormalX=0 NormalY=0 NormalZ=1 AngleXU=2e-16 Radius=0.186667 StartAngle=0 EndAngle=1.5708
    g92: LineSegment StartX=113.613 StartY=24.825 StartZ=0 EndX=111.5 EndY=24.825 EndZ=0
    g93: ArcOfCircle CenterX=188.8 CenterY=78.575 CenterZ=0 NormalX=0 NormalY=0 NormalZ=1 AngleXU=2e-16 Radius=0.186667 StartAngle=1.5708 EndAngle=4.71239
    g94: ArcOfCircle CenterX=113.8 CenterY=24.825 CenterZ=0 NormalX=0 NormalY=0 NormalZ=1 AngleXU=-3.14159 Radius=0.186667 StartAngle=4.71239 EndAngle=6.28319
    g95: LineSegment StartX=188.8 StartY=78.3883 StartZ=0 EndX=188.8 EndY=41.4117 EndZ=0
    g96: ArcOfCircle CenterX=113.8 CenterY=24.825 CenterZ=0 NormalX=0 NormalY=0 NormalZ=1 AngleXU=-3.14159 Radius=0.186667 StartAngle=1.5708 EndAngle=4.71239
    g97: ArcOfCircle CenterX=188.8 CenterY=41.225 CenterZ=0 NormalX=0 NormalY=0 NormalZ=1 AngleXU=2e-16 Radius=0.186667 StartAngle=1.5708 EndAngle=4.71239
    g98: LineSegment StartX=113.8 StartY=12.9 StartZ=0 EndX=113.8 EndY=24.6383 EndZ=0
    g99: ArcOfCircle CenterX=188.8 CenterY=41.225 CenterZ=0 NormalX=0 NormalY=0 NormalZ=1 AngleXU=2e-16 Radius=0.186667 StartAngle=4.71239 EndAngle=6.28319
    g100: LineSegment StartX=114.3 StartY=12.4 StartZ=0 EndX=113.8 EndY=12.9 EndZ=0
    g101: LineSegment StartX=188.987 StartY=41.225 StartZ=0 EndX=191.1 EndY=41.225 EndZ=0
    g102: LineSegment StartX=127.288 StartY=12.4 StartZ=0 EndX=114.3 EndY=12.4 EndZ=0
    g103: LineSegment StartX=191.1 StartY=41.225 StartZ=0 EndX=191.4 EndY=40.925 EndZ=0
    g104: ArcOfCircle CenterX=127.475 CenterY=12.4 CenterZ=0 NormalX=0 NormalY=0 NormalZ=1 AngleXU=-1.5708 Radius=0.186667 StartAngle=1.5708 EndAngle=4.71239
    g105: ArcOfCircle CenterX=127.475 CenterY=12.4 CenterZ=0 NormalX=0 NormalY=0 NormalZ=1 AngleXU=-1.5708 Radius=0.186667 StartAngle=0 EndAngle=1.5708
    g106: LineSegment StartX=191.4 StartY=31.375 StartZ=0 EndX=191.1 EndY=31.075 EndZ=0
    g107: LineSegment StartX=127.475 StartY=12.2133 StartZ=0 EndX=127.475 EndY=10.1 EndZ=0
    g108: LineSegment StartX=188.987 StartY=31.075 StartZ=0 EndX=191.1 EndY=31.075 EndZ=0
    g109: LineSegment StartX=127.775 StartY=9.8 StartZ=0 EndX=127.475 EndY=10.1 EndZ=0
    g110: ArcOfCircle CenterX=188.8 CenterY=31.075 CenterZ=0 NormalX=0 NormalY=0 NormalZ=1 AngleXU=2e-16 Radius=0.186667 StartAngle=0 EndAngle=1.5708
    g111: ArcOfCircle CenterX=188.8 CenterY=31.075 CenterZ=0 NormalX=0 NormalY=0 NormalZ=1 AngleXU=2e-16 Radius=0.186667 StartAngle=1.5708 EndAngle=4.71239
    g112: LineSegment StartX=137.625 StartY=10.1 StartZ=0 EndX=137.325 EndY=9.8 EndZ=0
    g113: LineSegment StartX=188.8 StartY=30.8883 StartZ=0 EndX=188.8 EndY=12.9 EndZ=0
    g114: LineSegment StartX=137.625 StartY=12.2133 StartZ=0 EndX=137.625 EndY=10.1 EndZ=0
    g115: LineSegment StartX=188.8 StartY=12.9 StartZ=0 EndX=188.3 EndY=12.4 EndZ=0
    g116: ArcOfCircle CenterX=137.625 CenterY=12.4 CenterZ=0 NormalX=0 NormalY=0 NormalZ=1 AngleXU=-1.5708 Radius=0.186667 StartAngle=4.71239 EndAngle=6.28319
    g117: LineSegment StartX=188.3 StartY=12.4 StartZ=0 EndX=175.312 EndY=12.4 EndZ=0
    g118: ArcOfCircle CenterX=137.625 CenterY=12.4 CenterZ=0 NormalX=0 NormalY=0 NormalZ=1 AngleXU=-1.5708 Radius=0.186667 StartAngle=1.5708 EndAngle=4.71239
    g119: ArcOfCircle CenterX=175.125 CenterY=12.4 CenterZ=0 NormalX=0 NormalY=0 NormalZ=1 AngleXU=-1.5708 Radius=0.186667 StartAngle=1.5708 EndAngle=4.71239
    g120: LineSegment StartX=164.788 StartY=12.4 StartZ=0 EndX=137.812 EndY=12.4 EndZ=0
    g121: ArcOfCircle CenterX=175.125 CenterY=12.4 CenterZ=0 NormalX=0 NormalY=0 NormalZ=1 AngleXU=-1.5708 Radius=0.186667 StartAngle=4.71239 EndAngle=6.28319
    g122: ArcOfCircle CenterX=164.975 CenterY=12.4 CenterZ=0 NormalX=0 NormalY=0 NormalZ=1 AngleXU=-1.5708 Radius=0.186667 StartAngle=1.5708 EndAngle=4.71239
    g123: LineSegment StartX=175.125 StartY=12.2133 StartZ=0 EndX=175.125 EndY=10.1 EndZ=0
    g124: ArcOfCircle CenterX=164.975 CenterY=12.4 CenterZ=0 NormalX=0 NormalY=0 NormalZ=1 AngleXU=-1.5708 Radius=0.186667 StartAngle=0 EndAngle=1.5708
    g125: LineSegment StartX=175.125 StartY=10.1 StartZ=0 EndX=174.825 EndY=9.8 EndZ=0
    g126: LineSegment StartX=164.975 StartY=12.2133 StartZ=0 EndX=164.975 EndY=10.1 EndZ=0
    g127: LineSegment StartX=165.275 StartY=9.8 StartZ=0 EndX=164.975 EndY=10.1 EndZ=0
    g128: LineSegment StartX=159.782 StartY=63.0476 StartZ=0 EndX=162.131 EndY=62.1926 EndZ=0
    g129: ArcOfCircle CenterX=160.592 CenterY=57.964 CenterZ=0 NormalX=0 NormalY=0 NormalZ=1 AngleXU=2e-16 Radius=4.5 StartAngle=5.93412 EndAngle=7.50492
    g130: LineSegment StartX=164.821 StartY=56.4249 StartZ=0 EndX=162.597 EndY=50.3169 EndZ=0
    g131: ArcOfCircle CenterX=158.369 CenterY=51.856 CenterZ=0 NormalX=0 NormalY=0 NormalZ=1 AngleXU=2e-16 Radius=4.5 StartAngle=4.36332 EndAngle=5.93412
    g132: LineSegment StartX=156.83 StartY=47.6273 StartZ=0 EndX=154.48 EndY=48.4824 EndZ=0
    g133: ArcOfCircle CenterX=156.02 CenterY=52.711 CenterZ=0 NormalX=0 NormalY=0 NormalZ=1 AngleXU=2e-16 Radius=4.5 StartAngle=2.79253 EndAngle=4.36332
    g134: LineSegment StartX=151.791 StartY=54.2501 StartZ=0 EndX=154.014 EndY=60.3581 EndZ=0
    g135: ArcOfCircle CenterX=158.243 CenterY=58.819 CenterZ=0 NormalX=0 NormalY=0 NormalZ=1 AngleXU=2e-16 Radius=4.5 StartAngle=1.22173 EndAngle=2.79253
    g136: LineSegment StartX=183.606 StartY=81.6897 StartZ=0 EndX=185.024 EndY=81.1732 EndZ=0
    g137: LineSegment StartX=185.024 StartY=81.1732 StartZ=0 EndX=180.92 EndY=69.8969 EndZ=0
    g138: LineSegment StartX=179.501 StartY=70.4134 StartZ=0 EndX=180.92 EndY=69.8969 EndZ=0
    g139: LineSegment StartX=183.606 StartY=81.6897 StartZ=0 EndX=179.501 EndY=70.4134 EndZ=0
    g140: LineSegment StartX=172.661 StartY=51.6195 StartZ=0 EndX=174.08 EndY=51.1031 EndZ=0
    g141: LineSegment StartX=174.08 StartY=51.1031 StartZ=0 EndX=169.976 EndY=39.8268 EndZ=0
    g142: LineSegment StartX=168.557 StartY=40.3432 StartZ=0 EndX=169.976 EndY=39.8268 EndZ=0
    g143: LineSegment StartX=172.661 StartY=51.6195 StartZ=0 EndX=168.557 EndY=40.3432 EndZ=0
    g144: LineSegment StartX=121.5 StartY=42.51 StartZ=0 EndX=121.5 EndY=41 EndZ=0
    g145: LineSegment StartX=121.5 StartY=42.51 StartZ=0 EndX=133.5 EndY=42.51 EndZ=0
    g146: LineSegment StartX=133.5 StartY=42.51 StartZ=0 EndX=133.5 EndY=41 EndZ=0
    g147: LineSegment StartX=121.5 StartY=41 StartZ=0 EndX=133.5 EndY=41 EndZ=0
    g148: ArcOfCircle CenterX=169.302 CenterY=53.7467 CenterZ=0 NormalX=0 NormalY=0 NormalZ=1 AngleXU=2e-16 Radius=2.5 StartAngle=5.93412 EndAngle=9.07571
    g149: LineSegment StartX=171.651 StartY=52.8917 StartZ=0 EndX=170.249 EndY=49.0389 EndZ=0
    g150: ArcOfCircle CenterX=167.899 CenterY=49.894 CenterZ=0 NormalX=0 NormalY=0 NormalZ=1 AngleXU=2e-16 Radius=2.5 StartAngle=2.79253 EndAngle=5.93412
    g151: LineSegment StartX=166.952 StartY=54.6018 StartZ=0 EndX=165.55 EndY=50.749 EndZ=0
  constraints (16):
    c: PointOnObject(g65,g27)
    c: PointOnObject(g68,g27)
    c: PointOnObject(g87,g31)
    c: PointOnObject(g90,g31)
    c: PointOnObject(g109,g35)
    c: PointOnObject(g112,g35)
    c: PointOnObject(g125,g35)
    c: PointOnObject(g127,g35)
    c: PointOnObject(g106,g39)
    c: PointOnObject(g103,g39)
    c: PointOnObject(g88,g39)
    c: PointOnObject(g85,g39)
    c: PointOnObject(g66,g43)
    c: PointOnObject(g45,g43)
    c: PointOnObject(g49,g25)
    c: PointOnObject(g52,g25)
FEATURE [Sketcher::SketchObject] Sketch002
  ArcFitTolerance = 1e-06
  FullyConstrained = false
  MakeInternals = false
  sketch-geometry (140):
    g0: LineSegment StartX=58.3 StartY=115 StartZ=0 EndX=8.1 EndY=115 EndZ=0
    g1: ArcOfCircle CenterX=58.3 CenterY=112.5 CenterZ=0 NormalX=0 NormalY=0 NormalZ=1 AngleXU=-3.14159 Radius=2.5 StartAngle=3.14159 EndAngle=4.71239
    g2: ArcOfCircle CenterX=8.1 CenterY=112.5 CenterZ=0 NormalX=0 NormalY=0 NormalZ=1 AngleXU=-3.14159 Radius=2.5 StartAngle=4.71239 EndAngle=6.28319
    g3: LineSegment StartX=60.8 StartY=103.131 StartZ=0 EndX=60.8 EndY=112.5 EndZ=0
    g4: LineSegment StartX=5.6 StartY=112.5 StartZ=0 EndX=5.6 EndY=7.3 EndZ=0
    g5: ArcOfCircle CenterX=58.3 CenterY=103.131 CenterZ=0 NormalX=0 NormalY=0 NormalZ=1 AngleXU=-3.14159 Radius=2.5 StartAngle=1.91986 EndAngle=3.14159
    g6: ArcOfCircle CenterX=8.1 CenterY=7.3 CenterZ=0 NormalX=0 NormalY=0 NormalZ=1 AngleXU=-3.14159 Radius=2.5 StartAngle=0 EndAngle=1.5708
    g7: LineSegment StartX=50.1871 StartY=97.5174 StartZ=0 EndX=59.1551 EndY=100.781 EndZ=0
    g8: LineSegment StartX=8.1 StartY=4.8 StartZ=0 EndX=93.3 EndY=4.8 EndZ=0
    g9: ArcOfCircle CenterX=51.0422 CenterY=95.1682 CenterZ=0 NormalX=0 NormalY=0 NormalZ=1 AngleXU=-3.14159 Radius=2.5 StartAngle=5.06145 EndAngle=6.63225
    g10: ArcOfCircle CenterX=93.3 CenterY=7.3 CenterZ=0 NormalX=0 NormalY=0 NormalZ=1 AngleXU=-3.14159 Radius=2.5 StartAngle=1.5708 EndAngle=3.14159
    g11: LineSegment StartX=62.403 StartY=56.6449 StartZ=0 EndX=48.6929 EndY=94.3131 EndZ=0
    g12: LineSegment StartX=95.8 StartY=7.3 StartZ=0 EndX=95.8 EndY=52.5 EndZ=0
    g13: ArcOfCircle CenterX=64.7523 CenterY=57.5 CenterZ=0 NormalX=0 NormalY=0 NormalZ=1 AngleXU=-3.14159 Radius=2.5 StartAngle=0.349066 EndAngle=1.5708
    g14: ArcOfCircle CenterX=93.3 CenterY=52.5 CenterZ=0 NormalX=0 NormalY=0 NormalZ=1 AngleXU=-3.14159 Radius=2.5 StartAngle=3.14159 EndAngle=4.71239
    g15: LineSegment StartX=93.3 StartY=55 StartZ=0 EndX=64.7523 EndY=55 EndZ=0
    g16: ArcOfCircle CenterX=55.367 CenterY=110.25 CenterZ=0 NormalX=0 NormalY=0 NormalZ=1 AngleXU=-3.14159 Radius=0.25 StartAngle=1.5708 EndAngle=2.61799
    g17: ArcOfCircle CenterX=55.8 CenterY=110 CenterZ=0 NormalX=0 NormalY=0 NormalZ=1 AngleXU=-3.14159 Radius=0.25 StartAngle=2.0944 EndAngle=5.75959
    g18: ArcOfCircle CenterX=56.05 CenterY=109.567 CenterZ=0 NormalX=0 NormalY=0 NormalZ=1 AngleXU=-3.14159 Radius=0.25 StartAngle=5.23599 EndAngle=6.28319
    g19: LineSegment StartX=55.8 StartY=104.993 StartZ=0 EndX=55.8 EndY=109.567 EndZ=0
    g20: ArcOfCircle CenterX=56.05 CenterY=104.993 CenterZ=0 NormalX=0 NormalY=0 NormalZ=1 AngleXU=-3.14159 Radius=0.25 StartAngle=0 EndAngle=1.0472
    g21: ArcOfCircle CenterX=55.8 CenterY=104.56 CenterZ=0 NormalX=0 NormalY=0 NormalZ=1 AngleXU=-3.14159 Radius=0.25 StartAngle=0.872665 EndAngle=4.18879
    g22: ArcOfCircle CenterX=55.4786 CenterY=104.177 CenterZ=0 NormalX=0 NormalY=0 NormalZ=1 AngleXU=-3.14159 Radius=0.25 StartAngle=4.01426 EndAngle=5.06145
    g23: LineSegment StartX=42.4721 StartY=99.7094 StartZ=0 EndX=55.3931 EndY=104.412 EndZ=0
    g24: ArcOfCircle CenterX=42.8142 CenterY=98.7697 CenterZ=0 NormalX=0 NormalY=0 NormalZ=1 AngleXU=-3.14159 Radius=1 StartAngle=5.06145 EndAngle=6.63225
    g25: LineSegment StartX=59.2612 StartY=50.658 StartZ=0 EndX=41.8745 EndY=98.4277 EndZ=0
    g26: ArcOfCircle CenterX=60.2009 CenterY=51 CenterZ=0 NormalX=0 NormalY=0 NormalZ=1 AngleXU=-3.14159 Radius=1 StartAngle=0.349066 EndAngle=1.5708
    g27: LineSegment StartX=90.367 StartY=50 StartZ=0 EndX=60.2009 EndY=50 EndZ=0
    g28: ArcOfCircle CenterX=90.367 CenterY=50.25 CenterZ=0 NormalX=0 NormalY=0 NormalZ=1 AngleXU=-3.14159 Radius=0.25 StartAngle=1.5708 EndAngle=2.61799
    g29: ArcOfCircle CenterX=90.8 CenterY=50 CenterZ=0 NormalX=0 NormalY=0 NormalZ=1 AngleXU=-3.14159 Radius=0.25 StartAngle=2.0944 EndAngle=5.75959
    g30: ArcOfCircle CenterX=91.05 CenterY=49.567 CenterZ=0 NormalX=0 NormalY=0 NormalZ=1 AngleXU=-3.14159 Radius=0.25 StartAngle=5.23599 EndAngle=6.28319
    g31: LineSegment StartX=90.8 StartY=10.233 StartZ=0 EndX=90.8 EndY=49.567 EndZ=0
    g32: ArcOfCircle CenterX=91.05 CenterY=10.233 CenterZ=0 NormalX=0 NormalY=0 NormalZ=1 AngleXU=-3.14159 Radius=0.25 StartAngle=0 EndAngle=1.0472
    g33: ArcOfCircle CenterX=90.8 CenterY=9.8 CenterZ=0 NormalX=0 NormalY=0 NormalZ=1 AngleXU=-3.14159 Radius=0.25 StartAngle=0.523599 EndAngle=4.18879
    g34: ArcOfCircle CenterX=90.367 CenterY=9.55 CenterZ=0 NormalX=0 NormalY=0 NormalZ=1 AngleXU=-3.14159 Radius=0.25 StartAngle=3.66519 EndAngle=4.71239
    g35: LineSegment StartX=11.033 StartY=9.8 StartZ=0 EndX=90.367 EndY=9.8 EndZ=0
    g36: ArcOfCircle CenterX=11.033 CenterY=9.55 CenterZ=0 NormalX=0 NormalY=0 NormalZ=1 AngleXU=-3.14159 Radius=0.25 StartAngle=4.71239 EndAngle=5.75959
    g37: ArcOfCircle CenterX=10.6 CenterY=9.8 CenterZ=0 NormalX=0 NormalY=0 NormalZ=1 AngleXU=-3.14159 Radius=0.25 StartAngle=5.23599 EndAngle=8.90118
    g38: ArcOfCircle CenterX=10.35 CenterY=10.233 CenterZ=0 NormalX=0 NormalY=0 NormalZ=1 AngleXU=-3.14159 Radius=0.25 StartAngle=2.0944 EndAngle=3.14159
    g39: LineSegment StartX=10.6 StartY=109.567 StartZ=0 EndX=10.6 EndY=10.233 EndZ=0
    g40: ArcOfCircle CenterX=10.35 CenterY=109.567 CenterZ=0 NormalX=0 NormalY=0 NormalZ=1 AngleXU=-3.14159 Radius=0.25 StartAngle=3.14159 EndAngle=4.18879
    g41: ArcOfCircle CenterX=10.6 CenterY=110 CenterZ=0 NormalX=0 NormalY=0 NormalZ=1 AngleXU=-3.14159 Radius=0.25 StartAngle=3.66519 EndAngle=7.33038
    g42: ArcOfCircle CenterX=11.033 CenterY=110.25 CenterZ=0 NormalX=0 NormalY=0 NormalZ=1 AngleXU=-3.14159 Radius=0.25 StartAngle=0.523599 EndAngle=1.5708
    g43: LineSegment StartX=55.367 StartY=110 StartZ=0 EndX=11.033 EndY=110 EndZ=0
    g44: LineSegment StartX=38.275 StartY=107.587 StartZ=0 EndX=38.275 EndY=109.7 EndZ=0
    g45: LineSegment StartX=38.275 StartY=109.7 StartZ=0 EndX=37.975 EndY=110 EndZ=0
    g46: ArcOfCircle CenterX=38.275 CenterY=107.4 CenterZ=0 NormalX=0 NormalY=0 NormalZ=1 AngleXU=1.5708 Radius=0.186667 StartAngle=0 EndAngle=1.5708
    g47: ArcOfCircle CenterX=38.275 CenterY=107.4 CenterZ=0 NormalX=0 NormalY=0 NormalZ=1 AngleXU=1.5708 Radius=0.186667 StartAngle=1.5708 EndAngle=4.71239
    g48: LineSegment StartX=28.425 StartY=110 StartZ=0 EndX=28.125 EndY=109.7 EndZ=0
    g49: LineSegment StartX=53.2 StartY=107.4 StartZ=0 EndX=38.4617 EndY=107.4 EndZ=0
    g50: LineSegment StartX=28.125 StartY=107.587 StartZ=0 EndX=28.125 EndY=109.7 EndZ=0
    g51: LineSegment StartX=53.2 StartY=106.381 StartZ=0 EndX=53.2 EndY=107.4 EndZ=0
    g52: ArcOfCircle CenterX=28.125 CenterY=107.4 CenterZ=0 NormalX=0 NormalY=0 NormalZ=1 AngleXU=1.5708 Radius=0.186667 StartAngle=4.71239 EndAngle=6.28319
    g53: LineSegment StartX=38.2 StartY=100.921 StartZ=0 EndX=53.2 EndY=106.381 EndZ=0
    g54: ArcOfCircle CenterX=28.125 CenterY=107.4 CenterZ=0 NormalX=0 NormalY=0 NormalZ=1 AngleXU=1.5708 Radius=0.186667 StartAngle=1.5708 EndAngle=4.71239
    g55: LineSegment StartX=46.1405 StartY=79.105 StartZ=0 EndX=38.2 EndY=100.921 EndZ=0
    g56: LineSegment StartX=27.9383 StartY=107.4 StartZ=0 EndX=13.7 EndY=107.4 EndZ=0
    g57: ArcOfCircle CenterX=46.2043 CenterY=78.9296 CenterZ=0 NormalX=0 NormalY=0 NormalZ=1 AngleXU=0.349066 Radius=0.186667 StartAngle=1.5708 EndAngle=4.71239
    g58: LineSegment StartX=13.7 StartY=107.4 StartZ=0 EndX=13.2 EndY=106.9 EndZ=0
    g59: ArcOfCircle CenterX=46.2043 CenterY=78.9296 CenterZ=0 NormalX=0 NormalY=0 NormalZ=1 AngleXU=0.349066 Radius=0.186667 StartAngle=4.71239 EndAngle=6.28319
    g60: LineSegment StartX=13.2 StartY=106.9 StartZ=0 EndX=13.2 EndY=88.9117 EndZ=0
    g61: LineSegment StartX=46.3797 StartY=78.9934 StartZ=0 EndX=48.3656 EndY=79.7163 EndZ=0
    g62: ArcOfCircle CenterX=13.2 CenterY=88.725 CenterZ=0 NormalX=0 NormalY=0 NormalZ=1 AngleXU=3.14159 Radius=0.186667 StartAngle=1.5708 EndAngle=4.71239
    g63: LineSegment StartX=48.7501 StartY=79.5369 StartZ=0 EndX=48.3656 EndY=79.7163 EndZ=0
    g64: ArcOfCircle CenterX=13.2 CenterY=88.725 CenterZ=0 NormalX=0 NormalY=0 NormalZ=1 AngleXU=3.14159 Radius=0.186667 StartAngle=0 EndAngle=1.5708
    g65: LineSegment StartX=13.0133 StartY=88.725 StartZ=0 EndX=10.9 EndY=88.725 EndZ=0
    g66: LineSegment StartX=51.8371 StartY=70.1784 StartZ=0 EndX=52.0164 EndY=70.5629 EndZ=0
    g67: LineSegment StartX=10.9 StartY=88.725 StartZ=0 EndX=10.6 EndY=88.425 EndZ=0
    g68: LineSegment StartX=49.8512 StartY=69.4556 StartZ=0 EndX=51.8371 EndY=70.1784 EndZ=0
    g69: ArcOfCircle CenterX=49.6758 CenterY=69.3917 CenterZ=0 NormalX=0 NormalY=0 NormalZ=1 AngleXU=0.349066 Radius=0.186667 StartAngle=0 EndAngle=1.5708
    g70: LineSegment StartX=10.6 StartY=78.875 StartZ=0 EndX=10.9 EndY=78.575 EndZ=0
    g71: ArcOfCircle CenterX=49.6758 CenterY=69.3917 CenterZ=0 NormalX=0 NormalY=0 NormalZ=1 AngleXU=0.349066 Radius=0.186667 StartAngle=1.5708 EndAngle=4.71239
    g72: LineSegment StartX=13.0133 StartY=78.575 StartZ=0 EndX=10.9 EndY=78.575 EndZ=0
    g73: LineSegment StartX=57.6802 StartY=47.4 StartZ=0 EndX=49.7397 EndY=69.2163 EndZ=0
    g74: ArcOfCircle CenterX=13.2 CenterY=78.575 CenterZ=0 NormalX=0 NormalY=0 NormalZ=1 AngleXU=3.14159 Radius=0.186667 StartAngle=4.71239 EndAngle=6.28319
    g75: LineSegment StartX=67.6784 StartY=47.4 StartZ=0 EndX=57.6802 EndY=47.4 EndZ=0
    g76: ArcOfCircle CenterX=13.2 CenterY=78.575 CenterZ=0 NormalX=0 NormalY=0 NormalZ=1 AngleXU=3.14159 Radius=0.186667 StartAngle=1.5708 EndAngle=4.71239
    g77: ArcOfCircle CenterX=67.8651 CenterY=47.4 CenterZ=0 NormalX=0 NormalY=0 NormalZ=1 AngleXU=1.5708 Radius=0.186667 StartAngle=1.5708 EndAngle=4.71239
    g78: LineSegment StartX=13.2 StartY=78.3883 StartZ=0 EndX=13.2 EndY=41.4117 EndZ=0
    g79: ArcOfCircle CenterX=67.8651 CenterY=47.4 CenterZ=0 NormalX=0 NormalY=0 NormalZ=1 AngleXU=1.5708 Radius=0.186667 StartAngle=4.71239 EndAngle=6.28319
    g80: ArcOfCircle CenterX=13.2 CenterY=41.225 CenterZ=0 NormalX=0 NormalY=0 NormalZ=1 AngleXU=3.14159 Radius=0.186667 StartAngle=1.5708 EndAngle=4.71239
    g81: LineSegment StartX=67.8651 StartY=47.5867 StartZ=0 EndX=67.8651 EndY=49.7 EndZ=0
    g82: ArcOfCircle CenterX=13.2 CenterY=41.225 CenterZ=0 NormalX=0 NormalY=0 NormalZ=1 AngleXU=3.14159 Radius=0.186667 StartAngle=0 EndAngle=1.5708
    g83: LineSegment StartX=68.1651 StartY=50 StartZ=0 EndX=67.8651 EndY=49.7 EndZ=0
    g84: LineSegment StartX=13.0133 StartY=41.225 StartZ=0 EndX=10.9 EndY=41.225 EndZ=0
    g85: LineSegment StartX=10.9 StartY=41.225 StartZ=0 EndX=10.6 EndY=40.925 EndZ=0
    g86: LineSegment StartX=78.0151 StartY=49.7 StartZ=0 EndX=77.7151 EndY=50 EndZ=0
    g87: LineSegment StartX=78.0151 StartY=47.5867 StartZ=0 EndX=78.0151 EndY=49.7 EndZ=0
    g88: LineSegment StartX=10.6 StartY=31.375 StartZ=0 EndX=10.9 EndY=31.075 EndZ=0
    g89: ArcOfCircle CenterX=78.0151 CenterY=47.4 CenterZ=0 NormalX=0 NormalY=0 NormalZ=1 AngleXU=1.5708 Radius=0.186667 StartAngle=0 EndAngle=1.5708
    g90: LineSegment StartX=13.0133 StartY=31.075 StartZ=0 EndX=10.9 EndY=31.075 EndZ=0
    g91: ArcOfCircle CenterX=78.0151 CenterY=47.4 CenterZ=0 NormalX=0 NormalY=0 NormalZ=1 AngleXU=1.5708 Radius=0.186667 StartAngle=1.5708 EndAngle=4.71239
    g92: ArcOfCircle CenterX=13.2 CenterY=31.075 CenterZ=0 NormalX=0 NormalY=0 NormalZ=1 AngleXU=3.14159 Radius=0.186667 StartAngle=4.71239 EndAngle=6.28319
    g93: LineSegment StartX=87.7 StartY=47.4 StartZ=0 EndX=78.2018 EndY=47.4 EndZ=0
    g94: ArcOfCircle CenterX=13.2 CenterY=31.075 CenterZ=0 NormalX=0 NormalY=0 NormalZ=1 AngleXU=3.14159 Radius=0.186667 StartAngle=1.5708 EndAngle=4.71239
    g95: LineSegment StartX=88.2 StartY=46.9 StartZ=0 EndX=87.7 EndY=47.4 EndZ=0
    g96: LineSegment StartX=13.2 StartY=30.8883 StartZ=0 EndX=13.2 EndY=12.9 EndZ=0
    g97: LineSegment StartX=88.2 StartY=35.1617 StartZ=0 EndX=88.2 EndY=46.9 EndZ=0
    g98: LineSegment StartX=13.2 StartY=12.9 StartZ=0 EndX=13.7 EndY=12.4 EndZ=0
    g99: ArcOfCircle CenterX=88.2 CenterY=34.975 CenterZ=0 NormalX=0 NormalY=0 NormalZ=1 AngleXU=-2e-16 Radius=0.186667 StartAngle=1.5708 EndAngle=4.71239
    g100: LineSegment StartX=13.7 StartY=12.4 StartZ=0 EndX=26.6883 EndY=12.4 EndZ=0
    g101: ArcOfCircle CenterX=88.2 CenterY=34.975 CenterZ=0 NormalX=0 NormalY=0 NormalZ=1 AngleXU=-2e-16 Radius=0.186667 StartAngle=4.71239 EndAngle=6.28319
    g102: ArcOfCircle CenterX=26.875 CenterY=12.4 CenterZ=0 NormalX=0 NormalY=0 NormalZ=1 AngleXU=-1.5708 Radius=0.186667 StartAngle=1.5708 EndAngle=4.71239
    g103: LineSegment StartX=88.3867 StartY=34.975 StartZ=0 EndX=90.5 EndY=34.975 EndZ=0
    g104: ArcOfCircle CenterX=26.875 CenterY=12.4 CenterZ=0 NormalX=0 NormalY=0 NormalZ=1 AngleXU=-1.5708 Radius=0.186667 StartAngle=0 EndAngle=1.5708
    g105: LineSegment StartX=90.8 StartY=34.675 StartZ=0 EndX=90.5 EndY=34.975 EndZ=0
    g106: LineSegment StartX=26.875 StartY=12.2133 StartZ=0 EndX=26.875 EndY=10.1 EndZ=0
    g107: LineSegment StartX=26.875 StartY=10.1 StartZ=0 EndX=27.175 EndY=9.8 EndZ=0
    g108: LineSegment StartX=90.5 StartY=24.825 StartZ=0 EndX=90.8 EndY=25.125 EndZ=0
    g109: LineSegment StartX=88.3867 StartY=24.825 StartZ=0 EndX=90.5 EndY=24.825 EndZ=0
    g110: LineSegment StartX=36.725 StartY=9.8 StartZ=0 EndX=37.025 EndY=10.1 EndZ=0
    g111: ArcOfCircle CenterX=88.2 CenterY=24.825 CenterZ=0 NormalX=0 NormalY=0 NormalZ=1 AngleXU=-2e-16 Radius=0.186667 StartAngle=0 EndAngle=1.5708
    g112: LineSegment StartX=37.025 StartY=12.2133 StartZ=0 EndX=37.025 EndY=10.1 EndZ=0
    g113: ArcOfCircle CenterX=88.2 CenterY=24.825 CenterZ=0 NormalX=0 NormalY=0 NormalZ=1 AngleXU=-2e-16 Radius=0.186667 StartAngle=1.5708 EndAngle=4.71239
    g114: ArcOfCircle CenterX=37.025 CenterY=12.4 CenterZ=0 NormalX=0 NormalY=0 NormalZ=1 AngleXU=-1.5708 Radius=0.186667 StartAngle=4.71239 EndAngle=6.28319
    g115: LineSegment StartX=88.2 StartY=12.9 StartZ=0 EndX=88.2 EndY=24.6383 EndZ=0
    g116: ArcOfCircle CenterX=37.025 CenterY=12.4 CenterZ=0 NormalX=0 NormalY=0 NormalZ=1 AngleXU=-1.5708 Radius=0.186667 StartAngle=1.5708 EndAngle=4.71239
    g117: LineSegment StartX=87.7 StartY=12.4 StartZ=0 EndX=88.2 EndY=12.9 EndZ=0
    g118: LineSegment StartX=37.2117 StartY=12.4 StartZ=0 EndX=64.1883 EndY=12.4 EndZ=0
    g119: LineSegment StartX=74.7117 StartY=12.4 StartZ=0 EndX=87.7 EndY=12.4 EndZ=0
    g120: ArcOfCircle CenterX=64.375 CenterY=12.4 CenterZ=0 NormalX=0 NormalY=0 NormalZ=1 AngleXU=-1.5708 Radius=0.186667 StartAngle=1.5708 EndAngle=4.71239
    g121: ArcOfCircle CenterX=74.525 CenterY=12.4 CenterZ=0 NormalX=0 NormalY=0 NormalZ=1 AngleXU=-1.5708 Radius=0.186667 StartAngle=1.5708 EndAngle=4.71239
    g122: ArcOfCircle CenterX=64.375 CenterY=12.4 CenterZ=0 NormalX=0 NormalY=0 NormalZ=1 AngleXU=-1.5708 Radius=0.186667 StartAngle=0 EndAngle=1.5708
    g123: ArcOfCircle CenterX=74.525 CenterY=12.4 CenterZ=0 NormalX=0 NormalY=0 NormalZ=1 AngleXU=-1.5708 Radius=0.186667 StartAngle=4.71239 EndAngle=6.28319
    g124: LineSegment StartX=64.375 StartY=12.2133 StartZ=0 EndX=64.375 EndY=10.1 EndZ=0
    g125: LineSegment StartX=74.525 StartY=12.2133 StartZ=0 EndX=74.525 EndY=10.1 EndZ=0
    g126: LineSegment StartX=64.375 StartY=10.1 StartZ=0 EndX=64.675 EndY=9.8 EndZ=0
    g127: LineSegment StartX=74.225 StartY=9.8 StartZ=0 EndX=74.525 EndY=10.1 EndZ=0
    g128: LineSegment StartX=18.3945 StartY=81.6897 StartZ=0 EndX=16.9756 EndY=81.1732 EndZ=0
    g129: LineSegment StartX=18.3945 StartY=81.6897 StartZ=0 EndX=22.4987 EndY=70.4134 EndZ=0
    g130: LineSegment StartX=22.4987 StartY=70.4134 StartZ=0 EndX=21.0798 EndY=69.8969 EndZ=0
    g131: LineSegment StartX=16.9756 StartY=81.1732 StartZ=0 EndX=21.0798 EndY=69.8969 EndZ=0
    g132: LineSegment StartX=29.3391 StartY=51.6195 StartZ=0 EndX=27.9202 EndY=51.1031 EndZ=0
    g133: LineSegment StartX=29.3391 StartY=51.6195 StartZ=0 EndX=33.4434 EndY=40.3432 EndZ=0
    g134: LineSegment StartX=33.4434 StartY=40.3432 StartZ=0 EndX=32.0244 EndY=39.8268 EndZ=0
    g135: LineSegment StartX=27.9202 StartY=51.1031 StartZ=0 EndX=32.0244 EndY=39.8268 EndZ=0
    g136: LineSegment StartX=68.5 StartY=42.51 StartZ=0 EndX=68.5 EndY=41 EndZ=0
    g137: LineSegment StartX=68.5 StartY=42.51 StartZ=0 EndX=80.5 EndY=42.51 EndZ=0
    g138: LineSegment StartX=80.5 StartY=42.51 StartZ=0 EndX=80.5 EndY=41 EndZ=0
    g139: LineSegment StartX=68.5 StartY=41 StartZ=0 EndX=80.5 EndY=41 EndZ=0
  constraints (16):
    c: PointOnObject(g45,g43)
    c: PointOnObject(g48,g43)
    c: PointOnObject(g67,g39)
    c: PointOnObject(g70,g39)
    c: PointOnObject(g85,g39)
    c: PointOnObject(g88,g39)
    c: PointOnObject(g110,g35)
    c: PointOnObject(g107,g35)
    c: PointOnObject(g127,g35)
    c: PointOnObject(g126,g35)
    c: PointOnObject(g105,g31)
    c: PointOnObject(g108,g31)
    c: PointOnObject(g86,g27)
    c: PointOnObject(g83,g27)
    c: PointOnObject(g63,g25)
    c: PointOnObject(g66,g25)
FEATURE [Sketcher::SketchObject] Sketch003
  ArcFitTolerance = 1e-06
  FullyConstrained = false
  MakeInternals = false
  sketch-geometry (122):
    g0: LineSegment StartX=114.2 StartY=280.2 StartZ=0 EndX=114.2 EndY=263.125 EndZ=0
    g1: LineSegment StartX=114.2 StartY=263.125 StartZ=0 EndX=114.7 EndY=262.625 EndZ=0
    g2: ArcOfCircle CenterX=114.6 CenterY=280.2 CenterZ=0 NormalX=0 NormalY=0 NormalZ=1 AngleXU=-3.14159 Radius=0.4 StartAngle=4.71239 EndAngle=6.28319
    g3: LineSegment StartX=114.7 StartY=262.625 StartZ=0 EndX=116.791 EndY=262.625 EndZ=0
    g4: LineSegment StartX=128.2 StartY=280.6 StartZ=0 EndX=114.6 EndY=280.6 EndZ=0
    g5: ArcOfCircle CenterX=116.965 CenterY=262.525 CenterZ=0 NormalX=0 NormalY=0 NormalZ=1 AngleXU=1e-16 Radius=0.200333 StartAngle=0 EndAngle=2.61799
    g6: ArcOfCircle CenterX=116.965 CenterY=262.525 CenterZ=0 NormalX=0 NormalY=0 NormalZ=1 AngleXU=1e-16 Radius=0.200333 StartAngle=5.23599 EndAngle=6.28319
    g7: ArcOfCircle CenterX=128.2 CenterY=281 CenterZ=0 NormalX=0 NormalY=0 NormalZ=1 AngleXU=-3.14159 Radius=0.4 StartAngle=1.5708 EndAngle=4.71239
    g8: LineSegment StartX=114.6 StartY=281.4 StartZ=0 EndX=128.2 EndY=281.4 EndZ=0
    g9: LineSegment StartX=117.065 StartY=252.949 StartZ=0 EndX=117.065 EndY=262.351 EndZ=0
    g10: ArcOfCircle CenterX=114.6 CenterY=281.8 CenterZ=0 NormalX=0 NormalY=0 NormalZ=1 AngleXU=-3.14159 Radius=0.4 StartAngle=0 EndAngle=1.5708
    g11: ArcOfCircle CenterX=116.965 CenterY=252.775 CenterZ=0 NormalX=0 NormalY=0 NormalZ=1 AngleXU=1e-16 Radius=0.200333 StartAngle=0 EndAngle=1.0472
    g12: ArcOfCircle CenterX=116.965 CenterY=252.775 CenterZ=0 NormalX=0 NormalY=0 NormalZ=1 AngleXU=1e-16 Radius=0.200333 StartAngle=3.66519 EndAngle=6.28319
    g13: LineSegment StartX=114.2 StartY=283.953 StartZ=0 EndX=114.2 EndY=281.8 EndZ=0
    g14: ArcOfCircle CenterX=114.6 CenterY=283.953 CenterZ=0 NormalX=0 NormalY=0 NormalZ=1 AngleXU=-3.14159 Radius=0.4 StartAngle=5.17604 EndAngle=6.28319
    g15: LineSegment StartX=114.7 StartY=252.675 StartZ=0 EndX=116.791 EndY=252.675 EndZ=0
    g16: LineSegment StartX=114.421 StartY=284.311 StartZ=0 EndX=116.2 EndY=285.2 EndZ=0
    g17: LineSegment StartX=114.7 StartY=252.675 StartZ=0 EndX=114.2 EndY=252.175 EndZ=0
    g18: LineSegment StartX=116.2 StartY=285.2 StartZ=0 EndX=116.2 EndY=284.2 EndZ=0
    g19: LineSegment StartX=114.2 StartY=252.175 StartZ=0 EndX=114.2 EndY=215.625 EndZ=0
    g20: LineSegment StartX=116.2 StartY=284.2 StartZ=0 EndX=119 EndY=284.2 EndZ=0
    g21: LineSegment StartX=114.2 StartY=215.625 StartZ=0 EndX=114.7 EndY=215.125 EndZ=0
    g22: LineSegment StartX=119 StartY=284.2 StartZ=0 EndX=119 EndY=286.2 EndZ=0
    g23: LineSegment StartX=114.7 StartY=215.125 StartZ=0 EndX=116.791 EndY=215.125 EndZ=0
    g24: LineSegment StartX=119 StartY=286.2 StartZ=0 EndX=126.413 EndY=284.214 EndZ=0
    g25: ArcOfCircle CenterX=116.965 CenterY=215.025 CenterZ=0 NormalX=0 NormalY=0 NormalZ=1 AngleXU=1e-16 Radius=0.200333 StartAngle=0 EndAngle=2.61799
    g26: ArcOfCircle CenterX=116.965 CenterY=215.025 CenterZ=0 NormalX=0 NormalY=0 NormalZ=1 AngleXU=1e-16 Radius=0.200333 StartAngle=5.23599 EndAngle=6.28319
    g27: ArcOfCircle CenterX=126.517 CenterY=284.6 CenterZ=0 NormalX=0 NormalY=0 NormalZ=1 AngleXU=-3.14159 Radius=0.4 StartAngle=1.309 EndAngle=1.5708
    g28: LineSegment StartX=126.517 StartY=284.2 StartZ=0 EndX=146.525 EndY=284.2 EndZ=0
    g29: LineSegment StartX=117.065 StartY=205.449 StartZ=0 EndX=117.065 EndY=214.851 EndZ=0
    g30: LineSegment StartX=147.025 StartY=283.7 StartZ=0 EndX=146.525 EndY=284.2 EndZ=0
    g31: ArcOfCircle CenterX=116.965 CenterY=205.275 CenterZ=0 NormalX=0 NormalY=0 NormalZ=1 AngleXU=1e-16 Radius=0.200333 StartAngle=0 EndAngle=1.0472
    g32: ArcOfCircle CenterX=116.965 CenterY=205.275 CenterZ=0 NormalX=0 NormalY=0 NormalZ=1 AngleXU=1e-16 Radius=0.200333 StartAngle=3.66519 EndAngle=6.28319
    g33: LineSegment StartX=147.025 StartY=283.7 StartZ=0 EndX=147.025 EndY=281.609 EndZ=0
    g34: ArcOfCircle CenterX=147.125 CenterY=281.435 CenterZ=0 NormalX=0 NormalY=0 NormalZ=1 AngleXU=-1.5708 Radius=0.200333 StartAngle=0 EndAngle=1.0472
    g35: ArcOfCircle CenterX=147.125 CenterY=281.435 CenterZ=0 NormalX=0 NormalY=0 NormalZ=1 AngleXU=-1.5708 Radius=0.200333 StartAngle=3.66519 EndAngle=6.28319
    g36: LineSegment StartX=114.7 StartY=205.175 StartZ=0 EndX=116.791 EndY=205.175 EndZ=0
    g37: LineSegment StartX=114.7 StartY=205.175 StartZ=0 EndX=114.2 EndY=204.675 EndZ=0
    g38: LineSegment StartX=147.299 StartY=281.335 StartZ=0 EndX=156.701 EndY=281.335 EndZ=0
    g39: LineSegment StartX=114.2 StartY=204.675 StartZ=0 EndX=114.2 EndY=187.6 EndZ=0
    g40: ArcOfCircle CenterX=156.875 CenterY=281.435 CenterZ=0 NormalX=0 NormalY=0 NormalZ=1 AngleXU=-1.5708 Radius=0.200333 StartAngle=0 EndAngle=2.61799
    g41: ArcOfCircle CenterX=156.875 CenterY=281.435 CenterZ=0 NormalX=0 NormalY=0 NormalZ=1 AngleXU=-1.5708 Radius=0.200333 StartAngle=5.23599 EndAngle=6.28319
    g42: ArcOfCircle CenterX=114.6 CenterY=187.6 CenterZ=0 NormalX=0 NormalY=0 NormalZ=1 AngleXU=-3.14159 Radius=0.4 StartAngle=0 EndAngle=1.5708
    g43: LineSegment StartX=114.6 StartY=187.2 StartZ=0 EndX=128.2 EndY=187.2 EndZ=0
    g44: LineSegment StartX=156.975 StartY=283.7 StartZ=0 EndX=156.975 EndY=281.609 EndZ=0
    g45: ArcOfCircle CenterX=128.2 CenterY=186.8 CenterZ=0 NormalX=0 NormalY=0 NormalZ=1 AngleXU=-3.14159 Radius=0.4 StartAngle=1.5708 EndAngle=4.71239
    g46: LineSegment StartX=157.475 StartY=284.2 StartZ=0 EndX=156.975 EndY=283.7 EndZ=0
    g47: LineSegment StartX=128.2 StartY=186.4 StartZ=0 EndX=114.6 EndY=186.4 EndZ=0
    g48: LineSegment StartX=157.475 StartY=284.2 StartZ=0 EndX=177.483 EndY=284.2 EndZ=0
    g49: ArcOfCircle CenterX=114.6 CenterY=186 CenterZ=0 NormalX=0 NormalY=0 NormalZ=1 AngleXU=-3.14159 Radius=0.4 StartAngle=4.71239 EndAngle=6.28319
    g50: ArcOfCircle CenterX=177.483 CenterY=284.6 CenterZ=0 NormalX=0 NormalY=0 NormalZ=1 AngleXU=-3.14159 Radius=0.4 StartAngle=1.5708 EndAngle=1.8326
    g51: LineSegment StartX=114.2 StartY=186 StartZ=0 EndX=114.2 EndY=183.847 EndZ=0
    g52: LineSegment StartX=177.587 StartY=284.214 StartZ=0 EndX=185 EndY=286.2 EndZ=0
    g53: ArcOfCircle CenterX=114.6 CenterY=183.847 CenterZ=0 NormalX=0 NormalY=0 NormalZ=1 AngleXU=-3.14159 Radius=0.4 StartAngle=0 EndAngle=1.10715
    g54: LineSegment StartX=185 StartY=286.2 StartZ=0 EndX=185 EndY=284.2 EndZ=0
    g55: LineSegment StartX=114.421 StartY=183.489 StartZ=0 EndX=116.2 EndY=182.6 EndZ=0
    g56: LineSegment StartX=187.8 StartY=284.2 StartZ=0 EndX=185 EndY=284.2 EndZ=0
    g57: LineSegment StartX=116.2 StartY=182.6 StartZ=0 EndX=116.2 EndY=183.6 EndZ=0
    g58: LineSegment StartX=187.8 StartY=285.2 StartZ=0 EndX=187.8 EndY=284.2 EndZ=0
    g59: LineSegment StartX=116.2 StartY=183.6 StartZ=0 EndX=119 EndY=183.6 EndZ=0
    g60: LineSegment StartX=189.579 StartY=284.311 StartZ=0 EndX=187.8 EndY=285.2 EndZ=0
    g61: LineSegment StartX=119 StartY=181.6 StartZ=0 EndX=119 EndY=183.6 EndZ=0
    g62: ArcOfCircle CenterX=189.4 CenterY=283.953 CenterZ=0 NormalX=0 NormalY=0 NormalZ=1 AngleXU=-3.14159 Radius=0.4 StartAngle=3.14159 EndAngle=4.24874
    g63: LineSegment StartX=126.413 StartY=183.586 StartZ=0 EndX=119 EndY=181.6 EndZ=0
    g64: LineSegment StartX=189.8 StartY=281.8 StartZ=0 EndX=189.8 EndY=283.953 EndZ=0
    g65: ArcOfCircle CenterX=126.517 CenterY=183.2 CenterZ=0 NormalX=0 NormalY=0 NormalZ=1 AngleXU=-3.14159 Radius=0.4 StartAngle=4.71239 EndAngle=4.97419
    g66: ArcOfCircle CenterX=189.4 CenterY=281.8 CenterZ=0 NormalX=0 NormalY=0 NormalZ=1 AngleXU=-3.14159 Radius=0.4 StartAngle=1.5708 EndAngle=3.14159
    g67: LineSegment StartX=177.483 StartY=183.6 StartZ=0 EndX=126.517 EndY=183.6 EndZ=0
    g68: LineSegment StartX=189.4 StartY=281.4 StartZ=0 EndX=175.8 EndY=281.4 EndZ=0
    g69: ArcOfCircle CenterX=177.483 CenterY=183.2 CenterZ=0 NormalX=0 NormalY=0 NormalZ=1 AngleXU=-3.14159 Radius=0.4 StartAngle=4.45059 EndAngle=4.71239
    g70: ArcOfCircle CenterX=175.8 CenterY=281 CenterZ=0 NormalX=0 NormalY=0 NormalZ=1 AngleXU=-3.14159 Radius=0.4 StartAngle=4.71239 EndAngle=7.85398
    g71: LineSegment StartX=185 StartY=181.6 StartZ=0 EndX=177.587 EndY=183.586 EndZ=0
    g72: LineSegment StartX=175.8 StartY=280.6 StartZ=0 EndX=189.4 EndY=280.6 EndZ=0
    g73: LineSegment StartX=185 StartY=183.6 StartZ=0 EndX=185 EndY=181.6 EndZ=0
    g74: ArcOfCircle CenterX=189.4 CenterY=280.2 CenterZ=0 NormalX=0 NormalY=0 NormalZ=1 AngleXU=-3.14159 Radius=0.4 StartAngle=3.14159 EndAngle=4.71239
    g75: LineSegment StartX=187.8 StartY=183.6 StartZ=0 EndX=185 EndY=183.6 EndZ=0
    g76: LineSegment StartX=189.8 StartY=263.125 StartZ=0 EndX=189.8 EndY=280.2 EndZ=0
    g77: LineSegment StartX=187.8 StartY=182.6 StartZ=0 EndX=187.8 EndY=183.6 EndZ=0
    g78: LineSegment StartX=189.3 StartY=262.625 StartZ=0 EndX=189.8 EndY=263.125 EndZ=0
    g79: LineSegment StartX=189.579 StartY=183.489 StartZ=0 EndX=187.8 EndY=182.6 EndZ=0
    g80: LineSegment StartX=187.209 StartY=262.625 StartZ=0 EndX=189.3 EndY=262.625 EndZ=0
    g81: ArcOfCircle CenterX=189.4 CenterY=183.847 CenterZ=0 NormalX=0 NormalY=0 NormalZ=1 AngleXU=-3.14159 Radius=0.4 StartAngle=2.03444 EndAngle=3.14159
    g82: ArcOfCircle CenterX=187.035 CenterY=262.525 CenterZ=0 NormalX=0 NormalY=0 NormalZ=1 AngleXU=1e-16 Radius=0.200333 StartAngle=0.523599 EndAngle=4.18879
    g83: LineSegment StartX=189.8 StartY=183.847 StartZ=0 EndX=189.8 EndY=186 EndZ=0
    g84: LineSegment StartX=186.935 StartY=252.949 StartZ=0 EndX=186.935 EndY=262.351 EndZ=0
    g85: ArcOfCircle CenterX=189.4 CenterY=186 CenterZ=0 NormalX=0 NormalY=0 NormalZ=1 AngleXU=-3.14159 Radius=0.4 StartAngle=3.14159 EndAngle=4.71239
    g86: ArcOfCircle CenterX=187.035 CenterY=252.775 CenterZ=0 NormalX=0 NormalY=0 NormalZ=1 AngleXU=1e-16 Radius=0.200333 StartAngle=2.0944 EndAngle=5.75959
    g87: LineSegment StartX=189.4 StartY=186.4 StartZ=0 EndX=175.8 EndY=186.4 EndZ=0
    g88: LineSegment StartX=187.209 StartY=252.675 StartZ=0 EndX=189.3 EndY=252.675 EndZ=0
    g89: ArcOfCircle CenterX=175.8 CenterY=186.8 CenterZ=0 NormalX=0 NormalY=0 NormalZ=1 AngleXU=-3.14159 Radius=0.4 StartAngle=4.71239 EndAngle=7.85398
    g90: LineSegment StartX=189.8 StartY=252.175 StartZ=0 EndX=189.3 EndY=252.675 EndZ=0
    g91: LineSegment StartX=175.8 StartY=187.2 StartZ=0 EndX=189.4 EndY=187.2 EndZ=0
    g92: LineSegment StartX=189.8 StartY=215.625 StartZ=0 EndX=189.8 EndY=252.175 EndZ=0
    g93: ArcOfCircle CenterX=189.4 CenterY=187.6 CenterZ=0 NormalX=0 NormalY=0 NormalZ=1 AngleXU=-3.14159 Radius=0.4 StartAngle=1.5708 EndAngle=3.14159
    g94: LineSegment StartX=189.3 StartY=215.125 StartZ=0 EndX=189.8 EndY=215.625 EndZ=0
    g95: LineSegment StartX=189.8 StartY=187.6 StartZ=0 EndX=189.8 EndY=204.675 EndZ=0
    g96: LineSegment StartX=187.209 StartY=215.125 StartZ=0 EndX=189.3 EndY=215.125 EndZ=0
    g97: LineSegment StartX=189.8 StartY=204.675 StartZ=0 EndX=189.3 EndY=205.175 EndZ=0
    g98: ArcOfCircle CenterX=187.035 CenterY=215.025 CenterZ=0 NormalX=0 NormalY=0 NormalZ=1 AngleXU=1e-16 Radius=0.200333 StartAngle=0.523599 EndAngle=4.18879
    g99: LineSegment StartX=187.209 StartY=205.175 StartZ=0 EndX=189.3 EndY=205.175 EndZ=0
    g100: LineSegment StartX=186.935 StartY=205.449 StartZ=0 EndX=186.935 EndY=214.851 EndZ=0
    g101: ArcOfCircle CenterX=187.035 CenterY=205.275 CenterZ=0 NormalX=0 NormalY=0 NormalZ=1 AngleXU=1e-16 Radius=0.200333 StartAngle=2.0944 EndAngle=5.75959
    g102: ArcOfCircle CenterX=135.61 CenterY=203 CenterZ=0 NormalX=0 NormalY=0 NormalZ=1 AngleXU=-3.14159 Radius=0.8 StartAngle=3.44888 EndAngle=6.60988
    g103: ArcOfCircle CenterX=112 CenterY=195 CenterZ=0 NormalX=0 NormalY=0 NormalZ=1 AngleXU=-3.14159 Radius=24.1285 StartAngle=2.81489 EndAngle=3.46829
    g104: ArcOfCircle CenterX=110.4 CenterY=195 CenterZ=0 NormalX=0 NormalY=0 NormalZ=1 AngleXU=-3.14159 Radius=27.2489 StartAngle=2.83431 EndAngle=3.44888
    g105: ArcOfCircle CenterX=135.61 CenterY=187 CenterZ=0 NormalX=0 NormalY=0 NormalZ=1 AngleXU=-3.14159 Radius=0.8 StartAngle=5.95649 EndAngle=9.11749
    g106: ArcOfCircle CenterX=163.39 CenterY=188.31 CenterZ=0 NormalX=0 NormalY=0 NormalZ=1 AngleXU=-3.14159 Radius=2.11 StartAngle=1.5708 EndAngle=3.39711
    g107: ArcOfCircle CenterX=189 CenterY=195 CenterZ=0 NormalX=0 NormalY=0 NormalZ=1 AngleXU=-3.14159 Radius=24.3594 StartAngle=6.02767 EndAngle=6.5387
    g108: LineSegment StartX=163.39 StartY=186.2 StartZ=0 EndX=140.61 EndY=186.2 EndZ=0
    g109: ArcOfCircle CenterX=163.39 CenterY=201.69 CenterZ=0 NormalX=0 NormalY=0 NormalZ=1 AngleXU=-3.14159 Radius=2.11 StartAngle=2.88608 EndAngle=4.71239
    g110: ArcOfCircle CenterX=140.61 CenterY=188.31 CenterZ=0 NormalX=0 NormalY=0 NormalZ=1 AngleXU=-3.14159 Radius=2.11 StartAngle=6.02767 EndAngle=7.85398
    g111: LineSegment StartX=140.61 StartY=203.8 StartZ=0 EndX=163.39 EndY=203.8 EndZ=0
    g112: ArcOfCircle CenterX=115 CenterY=195 CenterZ=0 NormalX=0 NormalY=0 NormalZ=1 AngleXU=-3.14159 Radius=24.3594 StartAngle=2.88608 EndAngle=3.39711
    g113: ArcOfCircle CenterX=140.61 CenterY=201.69 CenterZ=0 NormalX=0 NormalY=0 NormalZ=1 AngleXU=-3.14159 Radius=2.11 StartAngle=4.71239 EndAngle=6.5387
    g114: ArcOfCircle CenterX=168.39 CenterY=203 CenterZ=0 NormalX=0 NormalY=0 NormalZ=1 AngleXU=-3.14159 Radius=0.8 StartAngle=2.81489 EndAngle=5.9759
    g115: ArcOfCircle CenterX=193.6 CenterY=195 CenterZ=0 NormalX=0 NormalY=0 NormalZ=1 AngleXU=-3.14159 Radius=27.2489 StartAngle=5.9759 EndAngle=6.59047
    g116: ArcOfCircle CenterX=192 CenterY=195 CenterZ=0 NormalX=0 NormalY=0 NormalZ=1 AngleXU=-3.14159 Radius=24.1285 StartAngle=5.95649 EndAngle=6.60988
    g117: ArcOfCircle CenterX=168.39 CenterY=187 CenterZ=0 NormalX=0 NormalY=0 NormalZ=1 AngleXU=-3.14159 Radius=0.8 StartAngle=0.307283 EndAngle=3.46829
    g118: LineSegment StartX=114.2 StartY=281.8 StartZ=0 EndX=114.2 EndY=280.2 EndZ=0
    g119: LineSegment StartX=114.2 StartY=187.6 StartZ=0 EndX=114.2 EndY=186 EndZ=0
    g120: LineSegment StartX=189.8 StartY=187.6 StartZ=0 EndX=189.8 EndY=186 EndZ=0
    g121: LineSegment StartX=189.8 StartY=281.8 StartZ=0 EndX=189.8 EndY=280.2 EndZ=0
  constraints (13):
    c: Tangent(g118,g10) = -1.5708
    c: Coincident(g118,g0)
    c: Vertical(g118)
    c: Coincident(g119,g39)
    c: Tangent(g119,g49) = -1.5708
    c: Vertical(g119)
    c: Coincident(g120,g93)
    c: Coincident(g120,g83)
    c: Vertical(g120)
    c: Tangent(g120,g85)
    c: Coincident(g121,g64)
    c: Tangent(g121,g74) = 1.5708
    c: Vertical(g121)
FEATURE [Sketcher::SketchObject] Sketch004
  ArcFitTolerance = 1e-06
  FullyConstrained = false
  MakeInternals = false
  sketch-geometry (80):
    g0: LineSegment StartX=13.7 StartY=256.036 StartZ=0 EndX=26.625 EndY=256.036 EndZ=0
    g1: LineSegment StartX=16 StartY=199.64 StartZ=0 EndX=13.7 EndY=199.64 EndZ=0
    g2: LineSegment StartX=13.7 StartY=199.64 StartZ=0 EndX=13.2 EndY=200.14 EndZ=0
    g3: LineSegment StartX=16 StartY=198.74 StartZ=0 EndX=16 EndY=199.64 EndZ=0
    g4: LineSegment StartX=13.2 StartY=200.14 StartZ=0 EndX=13.2 EndY=222.083 EndZ=0
    g5: LineSegment StartX=16 StartY=198.74 StartZ=0 EndX=16.5 EndY=198.24 EndZ=0
    g6: LineSegment StartX=13.7 StartY=222.583 StartZ=0 EndX=13.2 EndY=222.083 EndZ=0
    g7: LineSegment StartX=26.625 StartY=198.24 StartZ=0 EndX=16.5 EndY=198.24 EndZ=0
    g8: LineSegment StartX=13.7 StartY=222.583 StartZ=0 EndX=15.7913 EndY=222.583 EndZ=0
    g9: ArcOfCircle CenterX=15.9648 CenterY=222.683 CenterZ=0 NormalX=0 NormalY=0 NormalZ=1 AngleXU=0 Radius=0.200333 StartAngle=3.66519 EndAngle=6.28319
    g10: LineSegment StartX=27.125 StartY=200.826 StartZ=0 EndX=27.125 EndY=198.74 EndZ=0
    g11: ArcOfCircle CenterX=15.9648 CenterY=222.683 CenterZ=0 NormalX=0 NormalY=0 NormalZ=1 AngleXU=0 Radius=0.200333 StartAngle=0 EndAngle=1.0472
    g12: ArcOfEllipse CenterX=27.2227 CenterY=201.006 CenterZ=0 NormalX=0 NormalY=0 NormalZ=1 MajorRadius=0.207869 MinorRadius=0.195333 AngleXU=1.5708 StartAngle=1.5708 EndAngle=2.61799
    g13: ArcOfEllipse CenterX=27.2227 CenterY=201.006 CenterZ=0 NormalX=0 NormalY=0 NormalZ=1 MajorRadius=0.207869 MinorRadius=0.195333 AngleXU=1.5708 StartAngle=5.23599 EndAngle=7.85398
    g14: LineSegment StartX=16.065 StartY=232.259 StartZ=0 EndX=16.065 EndY=222.856 EndZ=0
    g15: LineSegment StartX=36.8082 StartY=201.109 StartZ=0 EndX=27.3918 EndY=201.109 EndZ=0
    g16: ArcOfCircle CenterX=15.9648 CenterY=232.433 CenterZ=0 NormalX=0 NormalY=0 NormalZ=1 AngleXU=0 Radius=0.200333 StartAngle=5.23599 EndAngle=6.28319
    g17: ArcOfEllipse CenterX=36.9773 CenterY=201.006 CenterZ=0 NormalX=0 NormalY=0 NormalZ=1 MajorRadius=0.207869 MinorRadius=0.195333 AngleXU=1.5708 StartAngle=4.71239 EndAngle=7.33038
    g18: ArcOfEllipse CenterX=36.9773 CenterY=201.006 CenterZ=0 NormalX=0 NormalY=0 NormalZ=1 MajorRadius=0.207869 MinorRadius=0.195333 AngleXU=1.5708 StartAngle=3.66519 EndAngle=4.71239
    g19: ArcOfCircle CenterX=15.9648 CenterY=232.433 CenterZ=0 NormalX=0 NormalY=0 NormalZ=1 AngleXU=0 Radius=0.200333 StartAngle=0 EndAngle=2.61799
    g20: LineSegment StartX=37.075 StartY=200.826 StartZ=0 EndX=37.075 EndY=198.74 EndZ=0
    g21: LineSegment StartX=13.7 StartY=232.533 StartZ=0 EndX=15.7913 EndY=232.533 EndZ=0
    g22: LineSegment StartX=13.2 StartY=233.033 StartZ=0 EndX=13.7 EndY=232.533 EndZ=0
    g23: LineSegment StartX=64.4249 StartY=198.24 StartZ=0 EndX=37.575 EndY=198.24 EndZ=0
    g24: LineSegment StartX=13.2 StartY=233.033 StartZ=0 EndX=13.2 EndY=255.536 EndZ=0
    g25: LineSegment StartX=13.7 StartY=256.036 StartZ=0 EndX=13.2 EndY=255.536 EndZ=0
    g26: LineSegment StartX=64.925 StartY=200.826 StartZ=0 EndX=64.925 EndY=198.74 EndZ=0
    g27: ArcOfEllipse CenterX=65.0227 CenterY=201.006 CenterZ=0 NormalX=0 NormalY=0 NormalZ=1 MajorRadius=0.207869 MinorRadius=0.195333 AngleXU=1.5708 StartAngle=1.5708 EndAngle=2.61799
    g28: ArcOfEllipse CenterX=65.0227 CenterY=201.006 CenterZ=0 NormalX=0 NormalY=0 NormalZ=1 MajorRadius=0.207869 MinorRadius=0.195333 AngleXU=1.5708 StartAngle=5.23599 EndAngle=7.85398
    g29: LineSegment StartX=26.625 StartY=256.036 StartZ=0 EndX=27.125 EndY=255.536 EndZ=0
    g30: LineSegment StartX=74.6082 StartY=201.109 StartZ=0 EndX=65.1918 EndY=201.109 EndZ=0
    g31: LineSegment StartX=27.125 StartY=255.536 StartZ=0 EndX=27.125 EndY=253.445 EndZ=0
    g32: ArcOfEllipse CenterX=74.7773 CenterY=201.006 CenterZ=0 NormalX=0 NormalY=0 NormalZ=1 MajorRadius=0.207869 MinorRadius=0.195333 AngleXU=1.5708 StartAngle=4.71239 EndAngle=7.33038
    g33: ArcOfEllipse CenterX=74.7773 CenterY=201.006 CenterZ=0 NormalX=0 NormalY=0 NormalZ=1 MajorRadius=0.207869 MinorRadius=0.195333 AngleXU=1.5708 StartAngle=3.66519 EndAngle=4.71239
    g34: ArcOfCircle CenterX=27.2252 CenterY=253.271 CenterZ=0 NormalX=0 NormalY=0 NormalZ=1 AngleXU=-1.5708 Radius=0.200333 StartAngle=3.66519 EndAngle=6.28319
    g35: LineSegment StartX=74.875 StartY=200.826 StartZ=0 EndX=74.875 EndY=198.74 EndZ=0
    g36: ArcOfCircle CenterX=27.2252 CenterY=253.271 CenterZ=0 NormalX=0 NormalY=0 NormalZ=1 AngleXU=-1.5708 Radius=0.200333 StartAngle=0 EndAngle=1.0472
    g37: LineSegment StartX=27.3987 StartY=253.171 StartZ=0 EndX=36.8013 EndY=253.171 EndZ=0
    g38: LineSegment StartX=85.5 StartY=198.24 StartZ=0 EndX=75.375 EndY=198.24 EndZ=0
    g39: ArcOfCircle CenterX=36.9748 CenterY=253.271 CenterZ=0 NormalX=0 NormalY=0 NormalZ=1 AngleXU=-1.5708 Radius=0.200333 StartAngle=5.23599 EndAngle=6.28319
    g40: LineSegment StartX=85.5 StartY=198.24 StartZ=0 EndX=86 EndY=198.74 EndZ=0
    g41: ArcOfCircle CenterX=36.9748 CenterY=253.271 CenterZ=0 NormalX=0 NormalY=0 NormalZ=1 AngleXU=-1.5708 Radius=0.200333 StartAngle=0 EndAngle=2.61799
    g42: LineSegment StartX=86 StartY=199.64 StartZ=0 EndX=86 EndY=198.74 EndZ=0
    g43: LineSegment StartX=37.075 StartY=255.536 StartZ=0 EndX=37.075 EndY=253.445 EndZ=0
    g44: LineSegment StartX=88.3 StartY=199.64 StartZ=0 EndX=86 EndY=199.64 EndZ=0
    g45: LineSegment StartX=37.575 StartY=256.036 StartZ=0 EndX=37.075 EndY=255.536 EndZ=0
    g46: LineSegment StartX=88.3 StartY=199.64 StartZ=0 EndX=88.8 EndY=200.14 EndZ=0
    g47: LineSegment StartX=37.575 StartY=256.036 StartZ=0 EndX=64.425 EndY=256.036 EndZ=0
    g48: LineSegment StartX=88.8 StartY=222.083 StartZ=0 EndX=88.8 EndY=200.14 EndZ=0
    g49: LineSegment StartX=64.925 StartY=255.536 StartZ=0 EndX=64.425 EndY=256.036 EndZ=0
    g50: LineSegment StartX=88.8 StartY=222.083 StartZ=0 EndX=88.3 EndY=222.583 EndZ=0
    g51: LineSegment StartX=64.925 StartY=255.536 StartZ=0 EndX=64.925 EndY=253.445 EndZ=0
    g52: LineSegment StartX=86.2087 StartY=222.583 StartZ=0 EndX=88.3 EndY=222.583 EndZ=0
    g53: ArcOfCircle CenterX=65.0252 CenterY=253.271 CenterZ=0 NormalX=0 NormalY=0 NormalZ=1 AngleXU=-1.5708 Radius=0.200333 StartAngle=3.66519 EndAngle=6.28319
    g54: ArcOfCircle CenterX=86.0352 CenterY=222.683 CenterZ=0 NormalX=0 NormalY=0 NormalZ=1 AngleXU=0 Radius=0.200333 StartAngle=2.0944 EndAngle=5.75959
    g55: ArcOfCircle CenterX=65.0252 CenterY=253.271 CenterZ=0 NormalX=0 NormalY=0 NormalZ=1 AngleXU=-1.5708 Radius=0.200333 StartAngle=0 EndAngle=1.0472
    g56: LineSegment StartX=85.935 StartY=232.259 StartZ=0 EndX=85.935 EndY=222.856 EndZ=0
    g57: LineSegment StartX=65.1987 StartY=253.171 StartZ=0 EndX=74.6013 EndY=253.171 EndZ=0
    g58: ArcOfCircle CenterX=86.0352 CenterY=232.433 CenterZ=0 NormalX=0 NormalY=0 NormalZ=1 AngleXU=0 Radius=0.200333 StartAngle=0.523599 EndAngle=4.18879
    g59: ArcOfCircle CenterX=74.7748 CenterY=253.271 CenterZ=0 NormalX=0 NormalY=0 NormalZ=1 AngleXU=-1.5708 Radius=0.200333 StartAngle=5.23599 EndAngle=6.28319
    g60: LineSegment StartX=86.2087 StartY=232.533 StartZ=0 EndX=88.3 EndY=232.533 EndZ=0
    g61: ArcOfCircle CenterX=74.7748 CenterY=253.271 CenterZ=0 NormalX=0 NormalY=0 NormalZ=1 AngleXU=-1.5708 Radius=0.200333 StartAngle=0 EndAngle=2.61799
    g62: LineSegment StartX=88.3 StartY=232.533 StartZ=0 EndX=88.8 EndY=233.033 EndZ=0
    g63: LineSegment StartX=74.875 StartY=255.536 StartZ=0 EndX=74.875 EndY=253.445 EndZ=0
    g64: LineSegment StartX=88.8 StartY=255.536 StartZ=0 EndX=88.8 EndY=233.033 EndZ=0
    g65: LineSegment StartX=75.375 StartY=256.036 StartZ=0 EndX=74.875 EndY=255.536 EndZ=0
    g66: LineSegment StartX=88.8 StartY=255.536 StartZ=0 EndX=88.3 EndY=256.036 EndZ=0
    g67: LineSegment StartX=75.375 StartY=256.036 StartZ=0 EndX=88.3 EndY=256.036 EndZ=0
    g68: LineSegment StartX=49.5 StartY=213.752 StartZ=0 EndX=52.5 EndY=213.752 EndZ=0
    g69: ArcOfCircle CenterX=49.5 CenterY=211.752 CenterZ=0 NormalX=0 NormalY=0 NormalZ=1 AngleXU=0 Radius=2 StartAngle=1.5708 EndAngle=4.71239
    g70: ArcOfCircle CenterX=52.5 CenterY=211.752 CenterZ=0 NormalX=0 NormalY=0 NormalZ=1 AngleXU=0 Radius=2 StartAngle=4.71239 EndAngle=7.85398
    g71: LineSegment StartX=49.5 StartY=209.752 StartZ=0 EndX=52.5 EndY=209.752 EndZ=0
    g72: LineSegment [constr] StartX=16 StartY=198.74 StartZ=0 EndX=27.125 EndY=198.74 EndZ=0
    g73: LineSegment [constr] StartX=37.075 StartY=198.74 StartZ=0 EndX=64.925 EndY=198.74 EndZ=0
    g74: LineSegment [constr] StartX=74.875 StartY=198.74 StartZ=0 EndX=86 EndY=198.74 EndZ=0
    g75: LineSegment StartX=37.075 StartY=198.74 StartZ=0 EndX=37.575 EndY=198.24 EndZ=0
    g76: LineSegment StartX=64.925 StartY=198.74 StartZ=0 EndX=64.4249 EndY=198.24 EndZ=0
    g77: LineSegment StartX=74.875 StartY=198.74 StartZ=0 EndX=75.375 EndY=198.24 EndZ=0
    g78: LineSegment [constr] StartX=27.125 StartY=198.74 StartZ=0 EndX=37.075 EndY=198.74 EndZ=0
    g79: LineSegment StartX=27.125 StartY=198.74 StartZ=0 EndX=26.625 EndY=198.24 EndZ=0
  constraints (22):
    c: Coincident(g72,g3)
    c: Coincident(g74,g40)
    c: Horizontal(g72)
    c: Angle(g-1,g75) = -0.785398
    c: Coincident(g75,g73)
    c: Angle(g-1,g76) = -2.35619
    c: Coincident(g76,g73)
    c: Angle(g-1,g77) = -0.785398
    c: Coincident(g77,g74)
    c: Coincident(g38,g77)
    c: Coincident(g35,g74)
    c: Coincident(g26,g73)
    c: Coincident(g23,g76)
    c: Coincident(g23,g75)
    c: Coincident(g20,g73)
    c: Coincident(g78,g72)
    c: Coincident(g78,g20)
    c: Horizontal(g78)
    c: Angle(g-1,g79) = -2.35619
    c: Coincident(g79,g72)
    c: Coincident(g10,g72)
    c: Coincident(g7,g79)
FEATURE [Sketcher::SketchObject] Sketch005
  ArcFitTolerance = 1e-06
  FullyConstrained = false
  MakeInternals = false
  sketch-geometry (94):
    g0: LineSegment StartX=114.7 StartY=315.535 StartZ=0 EndX=116.791 EndY=315.535 EndZ=0
    g1: LineSegment StartX=114.2 StartY=305.085 StartZ=0 EndX=114.2 EndY=295.8 EndZ=0
    g2: LineSegment StartX=114.2 StartY=305.085 StartZ=0 EndX=114.7 EndY=305.585 EndZ=0
    g3: LineSegment StartX=114.7 StartY=295.3 StartZ=0 EndX=114.2 EndY=295.8 EndZ=0
    g4: LineSegment StartX=114.7 StartY=305.585 StartZ=0 EndX=116.791 EndY=305.585 EndZ=0
    g5: LineSegment StartX=114.7 StartY=295.3 StartZ=0 EndX=135.398 EndY=295.3 EndZ=0
    g6: ArcOfCircle CenterX=116.965 CenterY=305.685 CenterZ=0 NormalX=0 NormalY=0 NormalZ=1 AngleXU=0 Radius=0.200333 StartAngle=3.66519 EndAngle=6.28319
    g7: ArcOfCircle CenterX=135.585 CenterY=295.3 CenterZ=0 NormalX=0 NormalY=0 NormalZ=1 AngleXU=-1.5708 Radius=0.186667 StartAngle=1.5708 EndAngle=4.71239
    g8: ArcOfCircle CenterX=116.965 CenterY=305.685 CenterZ=0 NormalX=0 NormalY=0 NormalZ=1 AngleXU=0 Radius=0.200333 StartAngle=0 EndAngle=1.0472
    g9: ArcOfCircle CenterX=135.585 CenterY=295.3 CenterZ=0 NormalX=0 NormalY=0 NormalZ=1 AngleXU=-1.5708 Radius=0.186667 StartAngle=0 EndAngle=1.5708
    g10: LineSegment StartX=117.065 StartY=315.261 StartZ=0 EndX=117.065 EndY=305.859 EndZ=0
    g11: LineSegment StartX=135.585 StartY=295.113 StartZ=0 EndX=135.585 EndY=293 EndZ=0
    g12: ArcOfCircle CenterX=116.965 CenterY=315.435 CenterZ=0 NormalX=0 NormalY=0 NormalZ=1 AngleXU=0 Radius=0.200333 StartAngle=5.23599 EndAngle=6.28319
    g13: LineSegment StartX=136.085 StartY=292.5 StartZ=0 EndX=135.585 EndY=293 EndZ=0
    g14: ArcOfCircle CenterX=116.965 CenterY=315.435 CenterZ=0 NormalX=0 NormalY=0 NormalZ=1 AngleXU=0 Radius=0.200333 StartAngle=0 EndAngle=2.61799
    g15: LineSegment StartX=145.235 StartY=292.5 StartZ=0 EndX=136.085 EndY=292.5 EndZ=0
    g16: LineSegment StartX=145.735 StartY=293 StartZ=0 EndX=145.235 EndY=292.5 EndZ=0
    g17: LineSegment StartX=114.7 StartY=315.535 StartZ=0 EndX=114.2 EndY=316.035 EndZ=0
    g18: LineSegment StartX=145.735 StartY=295.113 StartZ=0 EndX=145.735 EndY=293 EndZ=0
    g19: LineSegment StartX=114.2 StartY=321.84 StartZ=0 EndX=114.2 EndY=316.035 EndZ=0
    g20: ArcOfCircle CenterX=145.735 CenterY=295.3 CenterZ=0 NormalX=0 NormalY=0 NormalZ=1 AngleXU=-1.5708 Radius=0.186667 StartAngle=4.71239 EndAngle=6.28319
    g21: LineSegment StartX=114.2 StartY=321.84 StartZ=0 EndX=115.2 EndY=322.84 EndZ=0
    g22: ArcOfCircle CenterX=145.735 CenterY=295.3 CenterZ=0 NormalX=0 NormalY=0 NormalZ=1 AngleXU=-1.5708 Radius=0.186667 StartAngle=1.5708 EndAngle=4.71239
    g23: LineSegment StartX=127.838 StartY=322.84 StartZ=0 EndX=115.2 EndY=322.84 EndZ=0
    g24: LineSegment StartX=145.922 StartY=295.3 StartZ=0 EndX=158.078 EndY=295.3 EndZ=0
    g25: ArcOfCircle CenterX=128.025 CenterY=322.84 CenterZ=0 NormalX=0 NormalY=0 NormalZ=1 AngleXU=1.5708 Radius=0.186667 StartAngle=1.5708 EndAngle=4.71239
    g26: ArcOfCircle CenterX=158.265 CenterY=295.3 CenterZ=0 NormalX=0 NormalY=0 NormalZ=1 AngleXU=-1.5708 Radius=0.186667 StartAngle=1.5708 EndAngle=4.71239
    g27: ArcOfCircle CenterX=128.025 CenterY=322.84 CenterZ=0 NormalX=0 NormalY=0 NormalZ=1 AngleXU=1.5708 Radius=0.186667 StartAngle=4.71239 EndAngle=6.28319
    g28: ArcOfCircle CenterX=158.265 CenterY=295.3 CenterZ=0 NormalX=0 NormalY=0 NormalZ=1 AngleXU=-1.5708 Radius=0.186667 StartAngle=0 EndAngle=1.5708
    g29: LineSegment StartX=128.025 StartY=323.027 StartZ=0 EndX=128.025 EndY=325.14 EndZ=0
    g30: LineSegment StartX=158.265 StartY=295.113 StartZ=0 EndX=158.265 EndY=293 EndZ=0
    g31: LineSegment StartX=128.025 StartY=325.14 StartZ=0 EndX=128.525 EndY=325.64 EndZ=0
    g32: LineSegment StartX=158.765 StartY=292.5 StartZ=0 EndX=158.265 EndY=293 EndZ=0
    g33: LineSegment StartX=128.525 StartY=325.64 StartZ=0 EndX=137.675 EndY=325.64 EndZ=0
    g34: LineSegment StartX=167.915 StartY=292.5 StartZ=0 EndX=158.765 EndY=292.5 EndZ=0
    g35: LineSegment StartX=137.675 StartY=325.64 StartZ=0 EndX=138.175 EndY=325.14 EndZ=0
    g36: LineSegment StartX=168.415 StartY=293 StartZ=0 EndX=167.915 EndY=292.5 EndZ=0
    g37: LineSegment StartX=138.175 StartY=323.027 StartZ=0 EndX=138.175 EndY=325.14 EndZ=0
    g38: LineSegment StartX=168.415 StartY=295.113 StartZ=0 EndX=168.415 EndY=293 EndZ=0
    g39: ArcOfCircle CenterX=138.175 CenterY=322.84 CenterZ=0 NormalX=0 NormalY=0 NormalZ=1 AngleXU=1.5708 Radius=0.186667 StartAngle=0 EndAngle=1.5708
    g40: ArcOfCircle CenterX=168.415 CenterY=295.3 CenterZ=0 NormalX=0 NormalY=0 NormalZ=1 AngleXU=-1.5708 Radius=0.186667 StartAngle=4.71239 EndAngle=6.28319
    g41: ArcOfCircle CenterX=138.175 CenterY=322.84 CenterZ=0 NormalX=0 NormalY=0 NormalZ=1 AngleXU=1.5708 Radius=0.186667 StartAngle=1.5708 EndAngle=4.71239
    g42: ArcOfCircle CenterX=168.415 CenterY=295.3 CenterZ=0 NormalX=0 NormalY=0 NormalZ=1 AngleXU=-1.5708 Radius=0.186667 StartAngle=1.5708 EndAngle=4.71239
    g43: LineSegment StartX=165.638 StartY=322.84 StartZ=0 EndX=138.362 EndY=322.84 EndZ=0
    g44: LineSegment StartX=168.602 StartY=295.3 StartZ=0 EndX=189.3 EndY=295.3 EndZ=0
    g45: ArcOfCircle CenterX=165.825 CenterY=322.84 CenterZ=0 NormalX=0 NormalY=0 NormalZ=1 AngleXU=1.5708 Radius=0.186667 StartAngle=1.5708 EndAngle=4.71239
    g46: LineSegment StartX=189.8 StartY=295.8 StartZ=0 EndX=189.3 EndY=295.3 EndZ=0
    g47: ArcOfCircle CenterX=165.825 CenterY=322.84 CenterZ=0 NormalX=0 NormalY=0 NormalZ=1 AngleXU=1.5708 Radius=0.186667 StartAngle=4.71239 EndAngle=6.28319
    g48: LineSegment StartX=189.8 StartY=295.8 StartZ=0 EndX=189.8 EndY=305.085 EndZ=0
    g49: LineSegment StartX=165.825 StartY=323.027 StartZ=0 EndX=165.825 EndY=325.14 EndZ=0
    g50: LineSegment StartX=189.3 StartY=305.585 StartZ=0 EndX=189.8 EndY=305.085 EndZ=0
    g51: LineSegment StartX=165.825 StartY=325.14 StartZ=0 EndX=166.325 EndY=325.64 EndZ=0
    g52: LineSegment StartX=187.209 StartY=305.585 StartZ=0 EndX=189.3 EndY=305.585 EndZ=0
    g53: LineSegment StartX=166.325 StartY=325.64 StartZ=0 EndX=175.475 EndY=325.64 EndZ=0
    g54: ArcOfCircle CenterX=187.035 CenterY=305.685 CenterZ=0 NormalX=0 NormalY=0 NormalZ=1 AngleXU=0 Radius=0.200333 StartAngle=2.0944 EndAngle=5.75959
    g55: LineSegment StartX=175.475 StartY=325.64 StartZ=0 EndX=175.975 EndY=325.14 EndZ=0
    g56: LineSegment StartX=186.935 StartY=315.261 StartZ=0 EndX=186.935 EndY=305.859 EndZ=0
    g57: LineSegment StartX=175.975 StartY=323.027 StartZ=0 EndX=175.975 EndY=325.14 EndZ=0
    g58: ArcOfCircle CenterX=187.035 CenterY=315.435 CenterZ=0 NormalX=0 NormalY=0 NormalZ=1 AngleXU=0 Radius=0.200333 StartAngle=0.523599 EndAngle=4.18879
    g59: ArcOfCircle CenterX=175.975 CenterY=322.84 CenterZ=0 NormalX=0 NormalY=0 NormalZ=1 AngleXU=1.5708 Radius=0.186667 StartAngle=0 EndAngle=1.5708
    g60: LineSegment StartX=187.209 StartY=315.535 StartZ=0 EndX=189.3 EndY=315.535 EndZ=0
    g61: ArcOfCircle CenterX=175.975 CenterY=322.84 CenterZ=0 NormalX=0 NormalY=0 NormalZ=1 AngleXU=1.5708 Radius=0.186667 StartAngle=1.5708 EndAngle=4.71239
    g62: LineSegment StartX=189.8 StartY=316.035 StartZ=0 EndX=189.3 EndY=315.535 EndZ=0
    g63: LineSegment StartX=189.3 StartY=322.84 StartZ=0 EndX=176.162 EndY=322.84 EndZ=0
    g64: LineSegment StartX=189.8 StartY=316.035 StartZ=0 EndX=189.8 EndY=322.34 EndZ=0
    g65: LineSegment StartX=189.3 StartY=322.84 StartZ=0 EndX=189.8 EndY=322.34 EndZ=0
    g66: Circle CenterX=151.985 CenterY=312.034 CenterZ=0 NormalX=0 NormalY=0 NormalZ=1 AngleXU=-3.14159 Radius=7.5
    g67: LineSegment StartX=171.565 StartY=305.01 StartZ=0 EndX=169.208 EndY=311.01 EndZ=0
    g68: ArcOfCircle CenterX=165.98 CenterY=302.816 CenterZ=0 NormalX=0 NormalY=0 NormalZ=1 AngleXU=-3.14159 Radius=6 StartAngle=5.91756 EndAngle=9.79911
    g69: LineSegment StartX=162.681 StartY=310.981 StartZ=0 EndX=160.377 EndY=304.961 EndZ=0
    g70: ArcOfCircle CenterX=165.98 CenterY=309.73 CenterZ=0 NormalX=0 NormalY=0 NormalZ=1 AngleXU=-3.14159 Radius=3.47209 StartAngle=3.51904 EndAngle=5.91448
    g71: Circle CenterX=179.04 CenterY=305.55 CenterZ=0 NormalX=0 NormalY=0 NormalZ=1 AngleXU=-3.14159 Radius=5
    g72: Circle CenterX=124.96 CenterY=305.45 CenterZ=0 NormalX=0 NormalY=0 NormalZ=1 AngleXU=-3.14159 Radius=5
    g73: Circle CenterX=134.982 CenterY=307.462 CenterZ=0 NormalX=0 NormalY=0 NormalZ=1 AngleXU=-3.14159 Radius=3
    g74: ArcOfCircle CenterX=140.57 CenterY=305.45 CenterZ=0 NormalX=0 NormalY=0 NormalZ=1 AngleXU=-3.14159 Radius=1.5 StartAngle=-1.8e-15 EndAngle=3.14159
    g75: LineSegment StartX=139.07 StartY=305.45 StartZ=0 EndX=139.07 EndY=307.95 EndZ=0
    g76: ArcOfCircle CenterX=140.57 CenterY=307.95 CenterZ=0 NormalX=0 NormalY=0 NormalZ=1 AngleXU=-3.14159 Radius=1.5 StartAngle=3.14159 EndAngle=6.28319
    g77: LineSegment StartX=142.07 StartY=305.45 StartZ=0 EndX=142.07 EndY=307.95 EndZ=0
    g78: LineSegment [constr] StartX=165.98 StartY=302.816 StartZ=0 EndX=165.98 EndY=309.73 EndZ=0
    g79: LineSegment [constr] StartX=165.98 StartY=302.816 StartZ=0 EndX=158.736 EndY=300.875 EndZ=0
    g80: LineSegment [constr] StartX=165.98 StartY=302.816 StartZ=0 EndX=173.224 EndY=300.875 EndZ=0
    g81: Circle [constr] CenterX=165.98 CenterY=302.816 CenterZ=0 NormalX=0 NormalY=0 NormalZ=1 AngleXU=0 Radius=7.5
    g82: LineSegment [constr] StartX=158.736 StartY=300.875 StartZ=0 EndX=154.872 EndY=299.84 EndZ=0
    g83: LineSegment [constr] StartX=173.224 StartY=300.875 StartZ=0 EndX=177.088 EndY=299.84 EndZ=0
    g84: LineSegment StartX=158.736 StartY=300.875 StartZ=0 EndX=158.658 EndY=301.165 EndZ=0
    g85: LineSegment StartX=158.658 StartY=301.165 StartZ=0 EndX=154.794 EndY=300.129 EndZ=0
    g86: LineSegment StartX=154.794 StartY=300.129 StartZ=0 EndX=154.949 EndY=299.55 EndZ=0
    g87: LineSegment StartX=154.949 StartY=299.55 StartZ=0 EndX=158.813 EndY=300.585 EndZ=0
    g88: LineSegment StartX=158.813 StartY=300.585 StartZ=0 EndX=158.736 EndY=300.875 EndZ=0
    g89: LineSegment StartX=173.224 StartY=300.875 StartZ=0 EndX=173.302 EndY=301.165 EndZ=0
    g90: LineSegment StartX=173.302 StartY=301.165 StartZ=0 EndX=177.166 EndY=300.129 EndZ=0
    g91: LineSegment StartX=177.166 StartY=300.129 StartZ=0 EndX=177.011 EndY=299.55 EndZ=0
    g92: LineSegment StartX=177.011 StartY=299.55 StartZ=0 EndX=173.147 EndY=300.585 EndZ=0
    g93: LineSegment StartX=173.147 StartY=300.585 StartZ=0 EndX=173.224 EndY=300.875 EndZ=0
  constraints (55):
    c: Coincident(g78,g68)
    c: Coincident(g78,g70)
    c: Vertical(g78)
    c: Coincident(g79,g68)
    c: Coincident(g80,g68)
    c: DistanceX(g68) = 160.377
    c: DistanceY(g68) = 304.961
    c: DistanceX(g67) = 171.565
    c: DistanceY(g67) = 305.01
    c: DistanceX(g67) = 169.208
    c: DistanceY(g67) = 311.01
    c: DistanceX(g70) = 162.741
    c: DistanceY(g70) = 310.981
    c: DistanceX(g68) = 165.98
    c: DistanceY(g68) = 302.816
    c: Angle(g78,g79) = 1.8326
    c: Angle(g80,g78) = 1.8326
    c: Coincident(g81,g68)
    c: PointOnObject(g79,g81)
    c: Diameter(g81) = 15
    c: PointOnObject(g80,g81)
    c: Distance(g82) = 4
    c: Coincident(g82,g79)
    c: Distance(g83) = 4
    c: Coincident(g83,g80)
    c: Parallel(g83,g80)
    c: Parallel(g79,g82)
    c: Coincident(g79,g84)
    c: Coincident(g84,g85)
    c: Coincident(g85,g86)
    c: Coincident(g86,g87)
    c: Coincident(g87,g88)
    c: Coincident(g88,g84)
    c: Coincident(g80,g89)
    c: Coincident(g89,g90)
    c: Coincident(g90,g91)
    c: Coincident(g91,g92)
    c: Coincident(g92,g93)
    c: Coincident(g93,g89)
    c: Perpendicular(g82,g84)
    c: Perpendicular(g85,g84)
    c: Perpendicular(g86,g85)
    c: Perpendicular(g87,g86)
    c: Perpendicular(g88,g87)
    c: Equal(g84,g88)
    c: PointOnObject(g82,g86)
    c: Distance(g85,g86) = 0.6
    c: Perpendicular(g93,g83)
    c: Perpendicular(g92,g93)
    c: Perpendicular(g91,g92)
    c: Perpendicular(g90,g91)
    c: Perpendicular(g89,g90)
    c: Equal(g89,g93)
    c: Equal(g84,g89)
    c: PointOnObject(g83,g91)
FEATURE [Sketcher::SketchObject] Sketch006
  ArcFitTolerance = 1e-06
  FullyConstrained = false
  MakeInternals = false
  sketch-geometry (132):
    g0: LineSegment StartX=167.715 StartY=121.6 StartZ=0 EndX=176.383 EndY=121.6 EndZ=0
    g1: LineSegment StartX=167.715 StartY=121.6 StartZ=0 EndX=167.215 EndY=122.1 EndZ=0
    g2: ArcOfCircle CenterX=176.383 CenterY=121.2 CenterZ=0 NormalX=0 NormalY=0 NormalZ=1 AngleXU=1.5708 Radius=0.4 StartAngle=6.02139 EndAngle=6.28319
    g3: LineSegment StartX=167.215 StartY=122.1 StartZ=0 EndX=167.215 EndY=124.191 EndZ=0
    g4: LineSegment StartX=176.487 StartY=121.586 StartZ=0 EndX=183.9 EndY=119.6 EndZ=0
    g5: ArcOfCircle CenterX=167.115 CenterY=124.365 CenterZ=0 NormalX=0 NormalY=0 NormalZ=1 AngleXU=1.5708 Radius=0.200333 StartAngle=0 EndAngle=1.0472
    g6: ArcOfCircle CenterX=167.115 CenterY=124.365 CenterZ=0 NormalX=0 NormalY=0 NormalZ=1 AngleXU=1.5708 Radius=0.200333 StartAngle=3.66519 EndAngle=6.28319
    g7: LineSegment StartX=183.9 StartY=119.6 StartZ=0 EndX=183.9 EndY=121.6 EndZ=0
    g8: LineSegment StartX=183.9 StartY=121.6 StartZ=0 EndX=186.7 EndY=121.6 EndZ=0
    g9: LineSegment StartX=166.941 StartY=124.465 StartZ=0 EndX=157.539 EndY=124.465 EndZ=0
    g10: LineSegment StartX=186.7 StartY=120.6 StartZ=0 EndX=186.7 EndY=121.6 EndZ=0
    g11: ArcOfCircle CenterX=157.365 CenterY=124.365 CenterZ=0 NormalX=0 NormalY=0 NormalZ=1 AngleXU=1.5708 Radius=0.200333 StartAngle=0 EndAngle=2.61799
    g12: ArcOfCircle CenterX=157.365 CenterY=124.365 CenterZ=0 NormalX=0 NormalY=0 NormalZ=1 AngleXU=1.5708 Radius=0.200333 StartAngle=5.23599 EndAngle=6.28319
    g13: LineSegment StartX=188.479 StartY=121.489 StartZ=0 EndX=186.7 EndY=120.6 EndZ=0
    g14: ArcOfCircle CenterX=188.3 CenterY=121.847 CenterZ=0 NormalX=0 NormalY=0 NormalZ=1 AngleXU=1.5708 Radius=0.4 StartAngle=3.60524 EndAngle=4.71239
    g15: LineSegment StartX=157.265 StartY=122.1 StartZ=0 EndX=157.265 EndY=124.191 EndZ=0
    g16: LineSegment StartX=188.7 StartY=121.847 StartZ=0 EndX=188.7 EndY=124 EndZ=0
    g17: LineSegment StartX=157.265 StartY=122.1 StartZ=0 EndX=156.765 EndY=121.6 EndZ=0
    g18: ArcOfCircle CenterX=188.3 CenterY=124 CenterZ=0 NormalX=0 NormalY=0 NormalZ=1 AngleXU=1.5708 Radius=0.4 StartAngle=4.71239 EndAngle=6.28319
    g19: LineSegment StartX=145.035 StartY=121.6 StartZ=0 EndX=156.765 EndY=121.6 EndZ=0
    g20: LineSegment StartX=188.3 StartY=124.4 StartZ=0 EndX=174.7 EndY=124.4 EndZ=0
    g21: LineSegment StartX=145.035 StartY=121.6 StartZ=0 EndX=144.535 EndY=122.1 EndZ=0
    g22: ArcOfCircle CenterX=174.7 CenterY=124.8 CenterZ=0 NormalX=0 NormalY=0 NormalZ=1 AngleXU=3.14159 Radius=0.4 StartAngle=4.71239 EndAngle=7.85398
    g23: LineSegment StartX=144.535 StartY=122.1 StartZ=0 EndX=144.535 EndY=124.191 EndZ=0
    g24: LineSegment StartX=174.7 StartY=125.2 StartZ=0 EndX=188.3 EndY=125.2 EndZ=0
    g25: ArcOfCircle CenterX=144.435 CenterY=124.365 CenterZ=0 NormalX=0 NormalY=0 NormalZ=1 AngleXU=1.5708 Radius=0.200333 StartAngle=0 EndAngle=1.0472
    g26: ArcOfCircle CenterX=144.435 CenterY=124.365 CenterZ=0 NormalX=0 NormalY=0 NormalZ=1 AngleXU=1.5708 Radius=0.200333 StartAngle=3.66519 EndAngle=6.28319
    g27: ArcOfCircle CenterX=188.3 CenterY=125.6 CenterZ=0 NormalX=0 NormalY=0 NormalZ=1 AngleXU=1.5708 Radius=0.4 StartAngle=3.14159 EndAngle=4.71239
    g28: LineSegment StartX=188.7 StartY=125.6 StartZ=0 EndX=188.7 EndY=136.425 EndZ=0
    g29: LineSegment StartX=144.261 StartY=124.465 StartZ=0 EndX=134.859 EndY=124.465 EndZ=0
    g30: LineSegment StartX=188.2 StartY=136.925 StartZ=0 EndX=188.7 EndY=136.425 EndZ=0
    g31: ArcOfCircle CenterX=134.685 CenterY=124.365 CenterZ=0 NormalX=0 NormalY=0 NormalZ=1 AngleXU=1.5708 Radius=0.200333 StartAngle=0 EndAngle=2.61799
    g32: ArcOfCircle CenterX=134.685 CenterY=124.365 CenterZ=0 NormalX=0 NormalY=0 NormalZ=1 AngleXU=1.5708 Radius=0.200333 StartAngle=5.23599 EndAngle=6.28319
    g33: LineSegment StartX=188.2 StartY=136.925 StartZ=0 EndX=186.109 EndY=136.925 EndZ=0
    g34: ArcOfCircle CenterX=185.935 CenterY=137.025 CenterZ=0 NormalX=0 NormalY=0 NormalZ=1 AngleXU=3.14159 Radius=0.200333 StartAngle=0 EndAngle=2.61799
    g35: ArcOfCircle CenterX=185.935 CenterY=137.025 CenterZ=0 NormalX=0 NormalY=0 NormalZ=1 AngleXU=3.14159 Radius=0.200333 StartAngle=5.23599 EndAngle=6.28319
    g36: LineSegment StartX=134.585 StartY=122.1 StartZ=0 EndX=134.585 EndY=124.191 EndZ=0
    g37: LineSegment StartX=134.585 StartY=122.1 StartZ=0 EndX=134.085 EndY=121.6 EndZ=0
    g38: LineSegment StartX=185.835 StartY=146.601 StartZ=0 EndX=185.835 EndY=137.199 EndZ=0
    g39: LineSegment StartX=125.417 StartY=121.6 StartZ=0 EndX=134.085 EndY=121.6 EndZ=0
    g40: ArcOfCircle CenterX=185.935 CenterY=146.775 CenterZ=0 NormalX=0 NormalY=0 NormalZ=1 AngleXU=3.14159 Radius=0.200333 StartAngle=0 EndAngle=1.0472
    g41: ArcOfCircle CenterX=185.935 CenterY=146.775 CenterZ=0 NormalX=0 NormalY=0 NormalZ=1 AngleXU=3.14159 Radius=0.200333 StartAngle=3.66519 EndAngle=6.28319
    g42: ArcOfCircle CenterX=125.417 CenterY=121.2 CenterZ=0 NormalX=0 NormalY=0 NormalZ=1 AngleXU=1.5708 Radius=0.4 StartAngle=0 EndAngle=0.261799
    g43: LineSegment StartX=117.9 StartY=119.6 StartZ=0 EndX=125.313 EndY=121.586 EndZ=0
    g44: LineSegment StartX=188.2 StartY=146.875 StartZ=0 EndX=186.109 EndY=146.875 EndZ=0
    g45: LineSegment StartX=117.9 StartY=121.6 StartZ=0 EndX=117.9 EndY=119.6 EndZ=0
    g46: LineSegment StartX=188.7 StartY=147.375 StartZ=0 EndX=188.2 EndY=146.875 EndZ=0
    g47: LineSegment StartX=115.1 StartY=121.6 StartZ=0 EndX=117.9 EndY=121.6 EndZ=0
    g48: LineSegment StartX=188.7 StartY=147.375 StartZ=0 EndX=188.7 EndY=158.2 EndZ=0
    g49: LineSegment StartX=115.1 StartY=120.6 StartZ=0 EndX=115.1 EndY=121.6 EndZ=0
    g50: ArcOfCircle CenterX=188.3 CenterY=158.2 CenterZ=0 NormalX=0 NormalY=0 NormalZ=1 AngleXU=1.5708 Radius=0.4 StartAngle=4.71239 EndAngle=6.28319
    g51: LineSegment StartX=113.321 StartY=121.489 StartZ=0 EndX=115.1 EndY=120.6 EndZ=0
    g52: LineSegment StartX=188.3 StartY=158.6 StartZ=0 EndX=174.7 EndY=158.6 EndZ=0
    g53: ArcOfCircle CenterX=113.5 CenterY=121.847 CenterZ=0 NormalX=0 NormalY=0 NormalZ=1 AngleXU=1.5708 Radius=0.4 StartAngle=1.5708 EndAngle=2.67795
    g54: ArcOfCircle CenterX=174.7 CenterY=159 CenterZ=0 NormalX=0 NormalY=0 NormalZ=1 AngleXU=3.14159 Radius=0.4 StartAngle=4.71239 EndAngle=7.85398
    g55: LineSegment StartX=113.1 StartY=124 StartZ=0 EndX=113.1 EndY=121.847 EndZ=0
    g56: LineSegment StartX=174.7 StartY=159.4 StartZ=0 EndX=188.3 EndY=159.4 EndZ=0
    g57: ArcOfCircle CenterX=113.5 CenterY=124 CenterZ=0 NormalX=0 NormalY=0 NormalZ=1 AngleXU=1.5708 Radius=0.4 StartAngle=0 EndAngle=1.5708
    g58: ArcOfCircle CenterX=188.3 CenterY=159.8 CenterZ=0 NormalX=0 NormalY=0 NormalZ=1 AngleXU=1.5708 Radius=0.4 StartAngle=3.14159 EndAngle=4.71239
    g59: LineSegment StartX=127.1 StartY=124.4 StartZ=0 EndX=113.5 EndY=124.4 EndZ=0
    g60: LineSegment StartX=188.7 StartY=159.8 StartZ=0 EndX=188.7 EndY=161.953 EndZ=0
    g61: ArcOfCircle CenterX=127.1 CenterY=124.8 CenterZ=0 NormalX=0 NormalY=0 NormalZ=1 AngleXU=3.14159 Radius=0.4 StartAngle=1.5708 EndAngle=4.71239
    g62: ArcOfCircle CenterX=188.3 CenterY=161.953 CenterZ=0 NormalX=0 NormalY=0 NormalZ=1 AngleXU=1.5708 Radius=0.4 StartAngle=4.71239 EndAngle=5.81954
    g63: LineSegment StartX=113.5 StartY=125.2 StartZ=0 EndX=127.1 EndY=125.2 EndZ=0
    g64: LineSegment StartX=188.479 StartY=162.311 StartZ=0 EndX=186.7 EndY=163.2 EndZ=0
    g65: ArcOfCircle CenterX=113.5 CenterY=125.6 CenterZ=0 NormalX=0 NormalY=0 NormalZ=1 AngleXU=1.5708 Radius=0.4 StartAngle=1.5708 EndAngle=3.14159
    g66: LineSegment StartX=186.7 StartY=163.2 StartZ=0 EndX=186.7 EndY=162.2 EndZ=0
    g67: LineSegment StartX=113.1 StartY=136.425 StartZ=0 EndX=113.1 EndY=125.6 EndZ=0
    g68: LineSegment StartX=186.7 StartY=162.2 StartZ=0 EndX=183.9 EndY=162.2 EndZ=0
    g69: LineSegment StartX=113.1 StartY=136.425 StartZ=0 EndX=113.6 EndY=136.925 EndZ=0
    g70: LineSegment StartX=183.9 StartY=162.2 StartZ=0 EndX=183.9 EndY=164.2 EndZ=0
    g71: LineSegment StartX=115.691 StartY=136.925 StartZ=0 EndX=113.6 EndY=136.925 EndZ=0
    g72: LineSegment StartX=183.9 StartY=164.2 StartZ=0 EndX=176.487 EndY=162.214 EndZ=0
    g73: ArcOfCircle CenterX=115.865 CenterY=137.025 CenterZ=0 NormalX=0 NormalY=0 NormalZ=1 AngleXU=3.14159 Radius=0.200333 StartAngle=0.523599 EndAngle=4.18879
    g74: ArcOfCircle CenterX=176.383 CenterY=162.6 CenterZ=0 NormalX=0 NormalY=0 NormalZ=1 AngleXU=1.5708 Radius=0.4 StartAngle=3.14159 EndAngle=3.40339
    g75: LineSegment StartX=115.965 StartY=146.601 StartZ=0 EndX=115.965 EndY=137.199 EndZ=0
    g76: LineSegment StartX=176.383 StartY=162.2 StartZ=0 EndX=167.715 EndY=162.2 EndZ=0
    g77: ArcOfCircle CenterX=115.865 CenterY=146.775 CenterZ=0 NormalX=0 NormalY=0 NormalZ=1 AngleXU=3.14159 Radius=0.200333 StartAngle=2.0944 EndAngle=5.75959
    g78: LineSegment StartX=167.215 StartY=161.7 StartZ=0 EndX=167.715 EndY=162.2 EndZ=0
    g79: LineSegment StartX=115.691 StartY=146.875 StartZ=0 EndX=113.6 EndY=146.875 EndZ=0
    g80: LineSegment StartX=167.215 StartY=161.7 StartZ=0 EndX=167.215 EndY=159.609 EndZ=0
    g81: LineSegment StartX=113.6 StartY=146.875 StartZ=0 EndX=113.1 EndY=147.375 EndZ=0
    g82: ArcOfCircle CenterX=167.115 CenterY=159.435 CenterZ=0 NormalX=0 NormalY=0 NormalZ=1 AngleXU=-1.5708 Radius=0.200333 StartAngle=0 EndAngle=2.61799
    g83: ArcOfCircle CenterX=167.115 CenterY=159.435 CenterZ=0 NormalX=0 NormalY=0 NormalZ=1 AngleXU=-1.5708 Radius=0.200333 StartAngle=5.23599 EndAngle=6.28319
    g84: LineSegment StartX=113.1 StartY=158.2 StartZ=0 EndX=113.1 EndY=147.375 EndZ=0
    g85: ArcOfCircle CenterX=113.5 CenterY=158.2 CenterZ=0 NormalX=0 NormalY=0 NormalZ=1 AngleXU=1.5708 Radius=0.4 StartAngle=0 EndAngle=1.5708
    g86: LineSegment StartX=157.539 StartY=159.335 StartZ=0 EndX=166.941 EndY=159.335 EndZ=0
    g87: LineSegment StartX=127.1 StartY=158.6 StartZ=0 EndX=113.5 EndY=158.6 EndZ=0
    g88: ArcOfCircle CenterX=157.365 CenterY=159.435 CenterZ=0 NormalX=0 NormalY=0 NormalZ=1 AngleXU=-1.5708 Radius=0.200333 StartAngle=0 EndAngle=1.0472
    g89: ArcOfCircle CenterX=157.365 CenterY=159.435 CenterZ=0 NormalX=0 NormalY=0 NormalZ=1 AngleXU=-1.5708 Radius=0.200333 StartAngle=3.66519 EndAngle=6.28319
    g90: ArcOfCircle CenterX=127.1 CenterY=159 CenterZ=0 NormalX=0 NormalY=0 NormalZ=1 AngleXU=3.14159 Radius=0.4 StartAngle=1.5708 EndAngle=4.71239
    g91: LineSegment StartX=113.5 StartY=159.4 StartZ=0 EndX=127.1 EndY=159.4 EndZ=0
    g92: LineSegment StartX=157.265 StartY=161.7 StartZ=0 EndX=157.265 EndY=159.609 EndZ=0
    g93: ArcOfCircle CenterX=113.5 CenterY=159.8 CenterZ=0 NormalX=0 NormalY=0 NormalZ=1 AngleXU=1.5708 Radius=0.4 StartAngle=1.5708 EndAngle=3.14159
    g94: LineSegment StartX=156.765 StartY=162.2 StartZ=0 EndX=157.265 EndY=161.7 EndZ=0
    g95: LineSegment StartX=113.1 StartY=161.953 StartZ=0 EndX=113.1 EndY=159.8 EndZ=0
    g96: LineSegment StartX=156.765 StartY=162.2 StartZ=0 EndX=145.035 EndY=162.2 EndZ=0
    g97: ArcOfCircle CenterX=113.5 CenterY=161.953 CenterZ=0 NormalX=0 NormalY=0 NormalZ=1 AngleXU=1.5708 Radius=0.4 StartAngle=0.463648 EndAngle=1.5708
    g98: LineSegment StartX=144.535 StartY=161.7 StartZ=0 EndX=145.035 EndY=162.2 EndZ=0
    g99: LineSegment StartX=113.321 StartY=162.311 StartZ=0 EndX=115.1 EndY=163.2 EndZ=0
    g100: LineSegment StartX=144.535 StartY=161.7 StartZ=0 EndX=144.535 EndY=159.609 EndZ=0
    g101: LineSegment StartX=115.1 StartY=162.2 StartZ=0 EndX=115.1 EndY=163.2 EndZ=0
    g102: ArcOfCircle CenterX=144.435 CenterY=159.435 CenterZ=0 NormalX=0 NormalY=0 NormalZ=1 AngleXU=-1.5708 Radius=0.200333 StartAngle=0 EndAngle=2.61799
    g103: ArcOfCircle CenterX=144.435 CenterY=159.435 CenterZ=0 NormalX=0 NormalY=0 NormalZ=1 AngleXU=-1.5708 Radius=0.200333 StartAngle=5.23599 EndAngle=6.28319
    g104: LineSegment StartX=117.9 StartY=162.2 StartZ=0 EndX=115.1 EndY=162.2 EndZ=0
    g105: LineSegment StartX=117.9 StartY=164.2 StartZ=0 EndX=117.9 EndY=162.2 EndZ=0
    g106: LineSegment StartX=134.859 StartY=159.335 StartZ=0 EndX=144.261 EndY=159.335 EndZ=0
    g107: LineSegment StartX=125.313 StartY=162.214 StartZ=0 EndX=117.9 EndY=164.2 EndZ=0
    g108: ArcOfCircle CenterX=134.685 CenterY=159.435 CenterZ=0 NormalX=0 NormalY=0 NormalZ=1 AngleXU=-1.5708 Radius=0.200333 StartAngle=0 EndAngle=1.0472
    g109: ArcOfCircle CenterX=134.685 CenterY=159.435 CenterZ=0 NormalX=0 NormalY=0 NormalZ=1 AngleXU=-1.5708 Radius=0.200333 StartAngle=3.66519 EndAngle=6.28319
    g110: ArcOfCircle CenterX=125.417 CenterY=162.6 CenterZ=0 NormalX=0 NormalY=0 NormalZ=1 AngleXU=1.5708 Radius=0.4 StartAngle=2.87979 EndAngle=3.14159
    g111: LineSegment StartX=134.085 StartY=162.2 StartZ=0 EndX=125.417 EndY=162.2 EndZ=0
    g112: LineSegment StartX=134.585 StartY=161.7 StartZ=0 EndX=134.585 EndY=159.609 EndZ=0
    g113: LineSegment StartX=134.085 StartY=162.2 StartZ=0 EndX=134.585 EndY=161.7 EndZ=0
    g114: Circle CenterX=163.7 CenterY=134.9 CenterZ=0 NormalX=0 NormalY=0 NormalZ=-1 AngleXU=0 Radius=8.5
    g115: LineSegment StartX=148.05 StartY=129.3 StartZ=0 EndX=153.75 EndY=129.3 EndZ=0
    g116: ArcOfCircle CenterX=153.75 CenterY=126.8 CenterZ=0 NormalX=0 NormalY=0 NormalZ=1 AngleXU=3.14159 Radius=2.5 StartAngle=1.5708 EndAngle=4.71239
    g117: ArcOfCircle CenterX=148.05 CenterY=126.8 CenterZ=0 NormalX=0 NormalY=0 NormalZ=1 AngleXU=3.14159 Radius=2.5 StartAngle=4.71239 EndAngle=7.85398
    g118: LineSegment StartX=148.05 StartY=124.3 StartZ=0 EndX=153.75 EndY=124.3 EndZ=0
    g119: LineSegment StartX=162.9 StartY=154.51 StartZ=0 EndX=174.9 EndY=154.51 EndZ=0
    g120: ArcOfCircle CenterX=174.9 CenterY=153.755 CenterZ=0 NormalX=0 NormalY=0 NormalZ=1 AngleXU=3.14159 Radius=0.755 StartAngle=1.5708 EndAngle=4.71239
    g121: ArcOfCircle CenterX=162.9 CenterY=153.755 CenterZ=0 NormalX=0 NormalY=0 NormalZ=1 AngleXU=3.14159 Radius=0.755 StartAngle=4.71239 EndAngle=7.85398
    g122: LineSegment StartX=162.9 StartY=153 StartZ=0 EndX=174.9 EndY=153 EndZ=0
    g123: Circle CenterX=138.1 CenterY=134.9 CenterZ=0 NormalX=0 NormalY=0 NormalZ=-1 AngleXU=0 Radius=8.5
    g124: LineSegment StartX=126.9 StartY=154.51 StartZ=0 EndX=138.9 EndY=154.51 EndZ=0
    g125: ArcOfCircle CenterX=138.9 CenterY=153.755 CenterZ=0 NormalX=0 NormalY=0 NormalZ=1 AngleXU=3.14159 Radius=0.755 StartAngle=1.5708 EndAngle=4.71239
    g126: ArcOfCircle CenterX=126.9 CenterY=153.755 CenterZ=0 NormalX=0 NormalY=0 NormalZ=1 AngleXU=3.14159 Radius=0.755 StartAngle=4.71239 EndAngle=7.85398
    g127: LineSegment StartX=126.9 StartY=153 StartZ=0 EndX=138.9 EndY=153 EndZ=0
    g128: LineSegment StartX=113.1 StartY=159.8 StartZ=0 EndX=113.1 EndY=158.2 EndZ=0
    g129: LineSegment StartX=188.7 StartY=159.8 StartZ=0 EndX=188.7 EndY=158.2 EndZ=0
    g130: LineSegment StartX=188.7 StartY=124 StartZ=0 EndX=188.7 EndY=125.6 EndZ=0
    g131: LineSegment StartX=113.1 StartY=125.6 StartZ=0 EndX=113.1 EndY=124 EndZ=0
  constraints (13):
    c: Tangent(g128,g93) = -1.5708
    c: Coincident(g128,g84)
    c: Vertical(g128)
    c: Coincident(g129,g58)
    c: Coincident(g129,g48)
    c: Vertical(g129)
    c: Coincident(g130,g16)
    c: Coincident(g130,g27)
    c: Vertical(g130)
    c: Tangent(g130,g18)
    c: Tangent(g131,g65) = -1.5708
    c: Coincident(g131,g55)
    c: Vertical(g131)
FEATURE [Sketcher::SketchObject] Sketch007
  ArcFitTolerance = 1e-06
  FullyConstrained = false
  MakeInternals = false
  sketch-geometry (68):
    g0: LineSegment StartX=13.7 StartY=259.7 StartZ=0 EndX=88.3 EndY=259.7 EndZ=0
    g1: LineSegment StartX=13.7 StartY=259.7 StartZ=0 EndX=13.2 EndY=260.2 EndZ=0
    g2: LineSegment StartX=88.3 StartY=259.7 StartZ=0 EndX=88.8 EndY=260.2 EndZ=0
    g3: LineSegment StartX=13.2 StartY=272.975 StartZ=0 EndX=13.2 EndY=260.2 EndZ=0
    g4: LineSegment StartX=88.8 StartY=260.2 StartZ=0 EndX=88.8 EndY=272.975 EndZ=0
    g5: LineSegment StartX=13.2 StartY=272.975 StartZ=0 EndX=13.7 EndY=273.475 EndZ=0
    g6: LineSegment StartX=88.8 StartY=272.975 StartZ=0 EndX=88.3 EndY=273.475 EndZ=0
    g7: LineSegment StartX=13.7 StartY=273.475 StartZ=0 EndX=15.7913 EndY=273.475 EndZ=0
    g8: LineSegment StartX=86.2087 StartY=273.475 StartZ=0 EndX=88.3 EndY=273.475 EndZ=0
    g9: ArcOfCircle CenterX=15.9648 CenterY=273.575 CenterZ=0 NormalX=0 NormalY=0 NormalZ=1 AngleXU=1e-16 Radius=0.200333 StartAngle=3.66519 EndAngle=6.28319
    g10: ArcOfCircle CenterX=86.0352 CenterY=273.575 CenterZ=0 NormalX=0 NormalY=0 NormalZ=1 AngleXU=1e-16 Radius=0.200333 StartAngle=2.0944 EndAngle=5.75959
    g11: ArcOfCircle CenterX=15.9648 CenterY=273.575 CenterZ=0 NormalX=0 NormalY=0 NormalZ=1 AngleXU=1e-16 Radius=0.200333 StartAngle=0 EndAngle=1.0472
    g12: LineSegment StartX=85.935 StartY=283.151 StartZ=0 EndX=85.935 EndY=273.749 EndZ=0
    g13: LineSegment StartX=16.065 StartY=283.151 StartZ=0 EndX=16.065 EndY=273.749 EndZ=0
    g14: ArcOfCircle CenterX=86.0352 CenterY=283.325 CenterZ=0 NormalX=0 NormalY=0 NormalZ=1 AngleXU=1e-16 Radius=0.200333 StartAngle=0.523599 EndAngle=4.18879
    g15: ArcOfCircle CenterX=15.9648 CenterY=283.325 CenterZ=0 NormalX=0 NormalY=0 NormalZ=1 AngleXU=1e-16 Radius=0.200333 StartAngle=5.23599 EndAngle=6.28319
    g16: LineSegment StartX=86.2087 StartY=283.425 StartZ=0 EndX=88.3 EndY=283.425 EndZ=0
    g17: ArcOfCircle CenterX=15.9648 CenterY=283.325 CenterZ=0 NormalX=0 NormalY=0 NormalZ=1 AngleXU=1e-16 Radius=0.200333 StartAngle=0 EndAngle=2.61799
    g18: LineSegment StartX=88.3 StartY=283.425 StartZ=0 EndX=88.8 EndY=283.925 EndZ=0
    g19: LineSegment StartX=13.7 StartY=283.425 StartZ=0 EndX=15.7913 EndY=283.425 EndZ=0
    g20: LineSegment StartX=88.8 StartY=283.925 StartZ=0 EndX=88.8 EndY=310.475 EndZ=0
    g21: LineSegment StartX=13.2 StartY=283.925 StartZ=0 EndX=13.7 EndY=283.425 EndZ=0
    g22: LineSegment StartX=88.8 StartY=310.475 StartZ=0 EndX=88.3 EndY=310.975 EndZ=0
    g23: LineSegment StartX=13.2 StartY=310.475 StartZ=0 EndX=13.2 EndY=283.925 EndZ=0
    g24: LineSegment StartX=86.2087 StartY=310.975 StartZ=0 EndX=88.3 EndY=310.975 EndZ=0
    g25: LineSegment StartX=13.7 StartY=310.975 StartZ=0 EndX=13.2 EndY=310.475 EndZ=0
    g26: ArcOfCircle CenterX=86.0352 CenterY=311.075 CenterZ=0 NormalX=0 NormalY=0 NormalZ=1 AngleXU=1e-16 Radius=0.200333 StartAngle=2.0944 EndAngle=5.75959
    g27: LineSegment StartX=13.7 StartY=310.975 StartZ=0 EndX=15.7913 EndY=310.975 EndZ=0
    g28: LineSegment StartX=85.935 StartY=320.651 StartZ=0 EndX=85.935 EndY=311.249 EndZ=0
    g29: ArcOfCircle CenterX=15.9648 CenterY=311.075 CenterZ=0 NormalX=0 NormalY=0 NormalZ=1 AngleXU=1e-16 Radius=0.200333 StartAngle=3.66519 EndAngle=6.28319
    g30: ArcOfCircle CenterX=86.0352 CenterY=320.825 CenterZ=0 NormalX=0 NormalY=0 NormalZ=1 AngleXU=1e-16 Radius=0.200333 StartAngle=0.523599 EndAngle=4.18879
    g31: ArcOfCircle CenterX=15.9648 CenterY=311.075 CenterZ=0 NormalX=0 NormalY=0 NormalZ=1 AngleXU=1e-16 Radius=0.200333 StartAngle=0 EndAngle=1.0472
    g32: LineSegment StartX=86.2087 StartY=320.925 StartZ=0 EndX=88.3 EndY=320.925 EndZ=0
    g33: LineSegment StartX=16.065 StartY=320.651 StartZ=0 EndX=16.065 EndY=311.249 EndZ=0
    g34: LineSegment StartX=88.3 StartY=320.925 StartZ=0 EndX=88.8 EndY=321.425 EndZ=0
    g35: ArcOfCircle CenterX=15.9648 CenterY=320.825 CenterZ=0 NormalX=0 NormalY=0 NormalZ=1 AngleXU=1e-16 Radius=0.200333 StartAngle=5.23599 EndAngle=6.28319
    g36: LineSegment StartX=88.8 StartY=321.425 StartZ=0 EndX=88.8 EndY=334.2 EndZ=0
    g37: ArcOfCircle CenterX=15.9648 CenterY=320.825 CenterZ=0 NormalX=0 NormalY=0 NormalZ=1 AngleXU=1e-16 Radius=0.200333 StartAngle=0 EndAngle=2.61799
    g38: LineSegment StartX=88.8 StartY=334.2 StartZ=0 EndX=88.3 EndY=334.7 EndZ=0
    g39: LineSegment StartX=13.7 StartY=320.925 StartZ=0 EndX=15.7913 EndY=320.925 EndZ=0
    g40: LineSegment StartX=88.3 StartY=334.7 StartZ=0 EndX=67.6017 EndY=334.7 EndZ=0
    g41: LineSegment StartX=13.2 StartY=321.425 StartZ=0 EndX=13.7 EndY=320.925 EndZ=0
    g42: ArcOfCircle CenterX=67.415 CenterY=334.7 CenterZ=0 NormalX=0 NormalY=0 NormalZ=1 AngleXU=1.5708 Radius=0.186667 StartAngle=1.5708 EndAngle=4.71239
    g43: LineSegment StartX=13.2 StartY=334.2 StartZ=0 EndX=13.2 EndY=321.425 EndZ=0
    g44: ArcOfCircle CenterX=67.415 CenterY=334.7 CenterZ=0 NormalX=0 NormalY=0 NormalZ=1 AngleXU=1.5708 Radius=0.186667 StartAngle=0 EndAngle=1.5708
    g45: LineSegment StartX=13.7 StartY=334.7 StartZ=0 EndX=13.2 EndY=334.2 EndZ=0
    g46: LineSegment StartX=67.415 StartY=334.887 StartZ=0 EndX=67.415 EndY=337 EndZ=0
    g47: LineSegment StartX=34.3983 StartY=334.7 StartZ=0 EndX=13.7 EndY=334.7 EndZ=0
    g48: LineSegment StartX=67.415 StartY=337 StartZ=0 EndX=66.915 EndY=337.5 EndZ=0
    g49: ArcOfCircle CenterX=34.585 CenterY=334.7 CenterZ=0 NormalX=0 NormalY=0 NormalZ=1 AngleXU=1.5708 Radius=0.186667 StartAngle=1.5708 EndAngle=4.71239
    g50: LineSegment StartX=57.765 StartY=337.5 StartZ=0 EndX=66.915 EndY=337.5 EndZ=0
    g51: ArcOfCircle CenterX=34.585 CenterY=334.7 CenterZ=0 NormalX=0 NormalY=0 NormalZ=1 AngleXU=1.5708 Radius=0.186667 StartAngle=4.71239 EndAngle=6.28319
    g52: LineSegment StartX=57.765 StartY=337.5 StartZ=0 EndX=57.265 EndY=337 EndZ=0
    g53: LineSegment StartX=34.585 StartY=334.887 StartZ=0 EndX=34.585 EndY=337 EndZ=0
    g54: LineSegment StartX=57.265 StartY=334.887 StartZ=0 EndX=57.265 EndY=337 EndZ=0
    g55: LineSegment StartX=35.085 StartY=337.5 StartZ=0 EndX=34.585 EndY=337 EndZ=0
    g56: ArcOfCircle CenterX=57.265 CenterY=334.7 CenterZ=0 NormalX=0 NormalY=0 NormalZ=1 AngleXU=1.5708 Radius=0.186667 StartAngle=4.71239 EndAngle=6.28319
    g57: LineSegment StartX=35.085 StartY=337.5 StartZ=0 EndX=44.235 EndY=337.5 EndZ=0
    g58: ArcOfCircle CenterX=57.265 CenterY=334.7 CenterZ=0 NormalX=0 NormalY=0 NormalZ=1 AngleXU=1.5708 Radius=0.186667 StartAngle=1.5708 EndAngle=4.71239
    g59: LineSegment StartX=44.735 StartY=337 StartZ=0 EndX=44.235 EndY=337.5 EndZ=0
    g60: LineSegment StartX=57.0783 StartY=334.7 StartZ=0 EndX=44.9217 EndY=334.7 EndZ=0
    g61: LineSegment StartX=44.735 StartY=334.887 StartZ=0 EndX=44.735 EndY=337 EndZ=0
    g62: ArcOfCircle CenterX=44.735 CenterY=334.7 CenterZ=0 NormalX=0 NormalY=0 NormalZ=1 AngleXU=1.5708 Radius=0.186667 StartAngle=1.5708 EndAngle=4.71239
    g63: ArcOfCircle CenterX=44.735 CenterY=334.7 CenterZ=0 NormalX=0 NormalY=0 NormalZ=1 AngleXU=1.5708 Radius=0.186667 StartAngle=0 EndAngle=1.5708
    g64: LineSegment StartX=52.4 StartY=307.701 StartZ=0 EndX=52.4 EndY=297.701 EndZ=0
    g65: LineSegment StartX=52.4 StartY=297.701 StartZ=0 EndX=49.6 EndY=297.701 EndZ=0
    g66: LineSegment StartX=49.6 StartY=297.701 StartZ=0 EndX=49.6 EndY=307.701 EndZ=0
    g67: LineSegment StartX=49.6 StartY=307.701 StartZ=0 EndX=52.4 EndY=307.701 EndZ=0
FEATURE [Sketcher::SketchObject] Sketch008
  ArcFitTolerance = 1e-06
  FullyConstrained = false
  MakeInternals = false
  sketch-geometry (62):
    g0: LineSegment StartX=88.3 StartY=135.725 StartZ=0 EndX=86.2087 EndY=135.725 EndZ=0
    g1: LineSegment StartX=13.2 StartY=159.5 StartZ=0 EndX=13.2 EndY=146.175 EndZ=0
    g2: LineSegment StartX=13.7 StartY=145.675 StartZ=0 EndX=13.2 EndY=146.175 EndZ=0
    g3: ArcOfCircle CenterX=13.6 CenterY=159.5 CenterZ=0 NormalX=0 NormalY=0 NormalZ=1 AngleXU=1.5708 Radius=0.4 StartAngle=0 EndAngle=1.5708
    g4: LineSegment StartX=15.7913 StartY=145.675 StartZ=0 EndX=13.7 EndY=145.675 EndZ=0
    g5: LineSegment StartX=27.2 StartY=159.9 StartZ=0 EndX=13.6 EndY=159.9 EndZ=0
    g6: ArcOfCircle CenterX=15.9648 CenterY=145.575 CenterZ=0 NormalX=0 NormalY=0 NormalZ=1 AngleXU=3.14159 Radius=0.200333 StartAngle=2.0944 EndAngle=5.75959
    g7: ArcOfCircle CenterX=27.2 CenterY=160.3 CenterZ=0 NormalX=0 NormalY=0 NormalZ=1 AngleXU=3.14159 Radius=0.4 StartAngle=1.5708 EndAngle=4.71239
    g8: LineSegment StartX=16.065 StartY=135.999 StartZ=0 EndX=16.065 EndY=145.401 EndZ=0
    g9: LineSegment StartX=13.6 StartY=160.7 StartZ=0 EndX=27.2 EndY=160.7 EndZ=0
    g10: ArcOfCircle CenterX=15.9648 CenterY=135.825 CenterZ=0 NormalX=0 NormalY=0 NormalZ=1 AngleXU=3.14159 Radius=0.200333 StartAngle=0.523599 EndAngle=4.18879
    g11: ArcOfCircle CenterX=13.6 CenterY=161.1 CenterZ=0 NormalX=0 NormalY=0 NormalZ=1 AngleXU=1.5708 Radius=0.4 StartAngle=1.5708 EndAngle=3.14159
    g12: LineSegment StartX=15.7913 StartY=135.725 StartZ=0 EndX=13.7 EndY=135.725 EndZ=0
    g13: LineSegment StartX=13.2 StartY=163.253 StartZ=0 EndX=13.2 EndY=161.1 EndZ=0
    g14: LineSegment StartX=13.2 StartY=135.225 StartZ=0 EndX=13.7 EndY=135.725 EndZ=0
    g15: ArcOfCircle CenterX=13.6 CenterY=163.253 CenterZ=0 NormalX=0 NormalY=0 NormalZ=1 AngleXU=1.5708 Radius=0.4 StartAngle=0.463648 EndAngle=1.5708
    g16: LineSegment StartX=13.2 StartY=135.225 StartZ=0 EndX=13.2 EndY=121.2 EndZ=0
    g17: LineSegment StartX=13.4211 StartY=163.611 StartZ=0 EndX=15.2 EndY=164.5 EndZ=0
    g18: LineSegment StartX=13.7 StartY=120.7 StartZ=0 EndX=13.2 EndY=121.2 EndZ=0
    g19: LineSegment StartX=15.2 StartY=164.5 StartZ=0 EndX=15.2 EndY=163.5 EndZ=0
    g20: LineSegment StartX=13.7 StartY=120.7 StartZ=0 EndX=45.7383 EndY=120.7 EndZ=0
    g21: LineSegment StartX=15.2 StartY=163.5 StartZ=0 EndX=18 EndY=163.5 EndZ=0
    g22: ArcOfCircle CenterX=45.925 CenterY=120.7 CenterZ=0 NormalX=0 NormalY=0 NormalZ=1 AngleXU=-1.5708 Radius=0.186667 StartAngle=1.5708 EndAngle=4.71239
    g23: LineSegment StartX=18 StartY=163.5 StartZ=0 EndX=18 EndY=165.5 EndZ=0
    g24: ArcOfCircle CenterX=45.925 CenterY=120.7 CenterZ=0 NormalX=0 NormalY=0 NormalZ=1 AngleXU=-1.5708 Radius=0.186667 StartAngle=0 EndAngle=1.5708
    g25: LineSegment StartX=18 StartY=165.5 StartZ=0 EndX=25.4132 EndY=163.514 EndZ=0
    g26: LineSegment StartX=45.925 StartY=120.513 StartZ=0 EndX=45.925 EndY=118.4 EndZ=0
    g27: ArcOfCircle CenterX=25.5168 CenterY=163.9 CenterZ=0 NormalX=0 NormalY=0 NormalZ=1 AngleXU=1.5708 Radius=0.4 StartAngle=2.87979 EndAngle=3.14159
    g28: LineSegment StartX=46.425 StartY=117.9 StartZ=0 EndX=45.925 EndY=118.4 EndZ=0
    g29: LineSegment StartX=25.5168 StartY=163.5 StartZ=0 EndX=76.4832 EndY=163.5 EndZ=0
    g30: LineSegment StartX=55.575 StartY=117.9 StartZ=0 EndX=46.425 EndY=117.9 EndZ=0
    g31: ArcOfCircle CenterX=76.4832 CenterY=163.9 CenterZ=0 NormalX=0 NormalY=0 NormalZ=1 AngleXU=1.5708 Radius=0.4 StartAngle=3.14159 EndAngle=3.40339
    g32: LineSegment StartX=56.075 StartY=118.4 StartZ=0 EndX=55.575 EndY=117.9 EndZ=0
    g33: LineSegment StartX=76.5868 StartY=163.514 StartZ=0 EndX=84 EndY=165.5 EndZ=0
    g34: LineSegment StartX=56.075 StartY=120.513 StartZ=0 EndX=56.075 EndY=118.4 EndZ=0
    g35: LineSegment StartX=84 StartY=165.5 StartZ=0 EndX=84 EndY=163.5 EndZ=0
    g36: ArcOfCircle CenterX=56.075 CenterY=120.7 CenterZ=0 NormalX=0 NormalY=0 NormalZ=1 AngleXU=-1.5708 Radius=0.186667 StartAngle=4.71239 EndAngle=6.28319
    g37: LineSegment StartX=86.8 StartY=163.5 StartZ=0 EndX=84 EndY=163.5 EndZ=0
    g38: ArcOfCircle CenterX=56.075 CenterY=120.7 CenterZ=0 NormalX=0 NormalY=0 NormalZ=1 AngleXU=-1.5708 Radius=0.186667 StartAngle=1.5708 EndAngle=4.71239
    g39: LineSegment StartX=86.8 StartY=164.5 StartZ=0 EndX=86.8 EndY=163.5 EndZ=0
    g40: LineSegment StartX=56.2617 StartY=120.7 StartZ=0 EndX=88.3 EndY=120.7 EndZ=0
    g41: LineSegment StartX=88.5789 StartY=163.611 StartZ=0 EndX=86.8 EndY=164.5 EndZ=0
    g42: LineSegment StartX=88.8 StartY=121.2 StartZ=0 EndX=88.3 EndY=120.7 EndZ=0
    g43: ArcOfCircle CenterX=88.4 CenterY=163.253 CenterZ=0 NormalX=0 NormalY=0 NormalZ=1 AngleXU=1.5708 Radius=0.4 StartAngle=4.71239 EndAngle=5.81954
    g44: LineSegment StartX=88.8 StartY=135.225 StartZ=0 EndX=88.8 EndY=121.2 EndZ=0
    g45: LineSegment StartX=88.8 StartY=161.1 StartZ=0 EndX=88.8 EndY=163.253 EndZ=0
    g46: LineSegment StartX=88.3 StartY=135.725 StartZ=0 EndX=88.8 EndY=135.225 EndZ=0
    g47: ArcOfCircle CenterX=88.4 CenterY=161.1 CenterZ=0 NormalX=0 NormalY=0 NormalZ=1 AngleXU=1.5708 Radius=0.4 StartAngle=3.14159 EndAngle=4.71239
    g48: LineSegment StartX=88.4 StartY=160.7 StartZ=0 EndX=74.8 EndY=160.7 EndZ=0
    g49: ArcOfCircle CenterX=86.0352 CenterY=135.825 CenterZ=0 NormalX=0 NormalY=0 NormalZ=1 AngleXU=3.14159 Radius=0.200333 StartAngle=0 EndAngle=2.61799
    g50: ArcOfCircle CenterX=74.8 CenterY=160.3 CenterZ=0 NormalX=0 NormalY=0 NormalZ=1 AngleXU=3.14159 Radius=0.4 StartAngle=4.71239 EndAngle=7.85398
    g51: ArcOfCircle CenterX=86.0352 CenterY=135.825 CenterZ=0 NormalX=0 NormalY=0 NormalZ=1 AngleXU=3.14159 Radius=0.200333 StartAngle=5.23599 EndAngle=6.28319
    g52: LineSegment StartX=74.8 StartY=159.9 StartZ=0 EndX=88.4 EndY=159.9 EndZ=0
    g53: LineSegment StartX=85.935 StartY=135.999 StartZ=0 EndX=85.935 EndY=145.401 EndZ=0
    g54: ArcOfCircle CenterX=88.4 CenterY=159.5 CenterZ=0 NormalX=0 NormalY=0 NormalZ=1 AngleXU=1.5708 Radius=0.4 StartAngle=4.71239 EndAngle=6.28319
    g55: ArcOfCircle CenterX=86.0352 CenterY=145.575 CenterZ=0 NormalX=0 NormalY=0 NormalZ=1 AngleXU=3.14159 Radius=0.200333 StartAngle=0 EndAngle=1.0472
    g56: LineSegment StartX=88.8 StartY=159.5 StartZ=0 EndX=88.8 EndY=146.175 EndZ=0
    g57: ArcOfCircle CenterX=86.0352 CenterY=145.575 CenterZ=0 NormalX=0 NormalY=0 NormalZ=1 AngleXU=3.14159 Radius=0.200333 StartAngle=3.66519 EndAngle=6.28319
    g58: LineSegment StartX=88.8 StartY=146.175 StartZ=0 EndX=88.3 EndY=145.675 EndZ=0
    g59: LineSegment StartX=88.3 StartY=145.675 StartZ=0 EndX=86.2087 EndY=145.675 EndZ=0
    g60: LineSegment StartX=13.2 StartY=161.1 StartZ=0 EndX=13.2 EndY=159.5 EndZ=0
    g61: LineSegment StartX=88.8 StartY=161.1 StartZ=0 EndX=88.8 EndY=159.5 EndZ=0
  constraints (6):
    c: Tangent(g60,g11) = -1.5708
    c: Coincident(g60,g1)
    c: Vertical(g60)
    c: Coincident(g61,g45)
    c: Tangent(g61,g54) = 1.5708
    c: Vertical(g61)
FEATURE [Sketcher::SketchObject] Sketch009
  ArcFitTolerance = 1e-06
  FullyConstrained = false
  MakeInternals = false
  sketch-geometry (28):
    g0: LineSegment StartX=13.7 StartY=194.601 StartZ=0 EndX=88.3 EndY=194.601 EndZ=0
    g1: LineSegment StartX=13.2 StartY=179.978 StartZ=0 EndX=13.2 EndY=194.101 EndZ=0
    g2: LineSegment StartX=13.2 StartY=179.978 StartZ=0 EndX=13.7 EndY=179.478 EndZ=0
    g3: LineSegment StartX=13.7 StartY=194.601 StartZ=0 EndX=13.2 EndY=194.101 EndZ=0
    g4: LineSegment StartX=26.8383 StartY=179.478 StartZ=0 EndX=13.7 EndY=179.478 EndZ=0
    g5: ArcOfCircle CenterX=27.025 CenterY=179.478 CenterZ=0 NormalX=0 NormalY=0 NormalZ=1 AngleXU=-1.5708 Radius=0.186667 StartAngle=1.5708 EndAngle=4.71239
    g6: LineSegment StartX=88.3 StartY=194.601 StartZ=0 EndX=88.8 EndY=194.101 EndZ=0
    g7: ArcOfCircle CenterX=27.025 CenterY=179.478 CenterZ=0 NormalX=0 NormalY=0 NormalZ=1 AngleXU=-1.5708 Radius=0.186667 StartAngle=0 EndAngle=1.5708
    g8: LineSegment StartX=88.8 StartY=194.101 StartZ=0 EndX=88.8 EndY=179.978 EndZ=0
    g9: LineSegment StartX=27.025 StartY=179.291 StartZ=0 EndX=27.025 EndY=177.178 EndZ=0
    g10: LineSegment StartX=88.8 StartY=179.978 StartZ=0 EndX=88.3 EndY=179.478 EndZ=0
    g11: LineSegment StartX=27.025 StartY=177.178 StartZ=0 EndX=27.525 EndY=176.678 EndZ=0
    g12: LineSegment StartX=88.3 StartY=179.478 StartZ=0 EndX=75.1617 EndY=179.478 EndZ=0
    g13: LineSegment StartX=27.525 StartY=176.678 StartZ=0 EndX=36.675 EndY=176.678 EndZ=0
    g14: ArcOfCircle CenterX=74.975 CenterY=179.478 CenterZ=0 NormalX=0 NormalY=0 NormalZ=1 AngleXU=-1.5708 Radius=0.186667 StartAngle=1.5708 EndAngle=4.71239
    g15: LineSegment StartX=36.675 StartY=176.678 StartZ=0 EndX=37.175 EndY=177.178 EndZ=0
    g16: ArcOfCircle CenterX=74.975 CenterY=179.478 CenterZ=0 NormalX=0 NormalY=0 NormalZ=1 AngleXU=-1.5708 Radius=0.186667 StartAngle=4.71239 EndAngle=6.28319
    g17: LineSegment StartX=37.175 StartY=179.291 StartZ=0 EndX=37.175 EndY=177.178 EndZ=0
    g18: LineSegment StartX=74.975 StartY=179.291 StartZ=0 EndX=74.975 EndY=177.178 EndZ=0
    g19: ArcOfCircle CenterX=37.175 CenterY=179.478 CenterZ=0 NormalX=0 NormalY=0 NormalZ=1 AngleXU=-1.5708 Radius=0.186667 StartAngle=4.71239 EndAngle=6.28319
    g20: LineSegment StartX=74.975 StartY=177.178 StartZ=0 EndX=74.475 EndY=176.678 EndZ=0
    g21: ArcOfCircle CenterX=37.175 CenterY=179.478 CenterZ=0 NormalX=0 NormalY=0 NormalZ=1 AngleXU=-1.5708 Radius=0.186667 StartAngle=1.5708 EndAngle=4.71239
    g22: LineSegment StartX=65.325 StartY=176.678 StartZ=0 EndX=74.475 EndY=176.678 EndZ=0
    g23: LineSegment StartX=64.6383 StartY=179.478 StartZ=0 EndX=37.3617 EndY=179.478 EndZ=0
    g24: LineSegment StartX=64.825 StartY=177.178 StartZ=0 EndX=65.325 EndY=176.678 EndZ=0
    g25: ArcOfCircle CenterX=64.825 CenterY=179.478 CenterZ=0 NormalX=0 NormalY=0 NormalZ=1 AngleXU=-1.5708 Radius=0.186667 StartAngle=1.5708 EndAngle=4.71239
    g26: LineSegment StartX=64.825 StartY=179.291 StartZ=0 EndX=64.825 EndY=177.178 EndZ=0
    g27: ArcOfCircle CenterX=64.825 CenterY=179.478 CenterZ=0 NormalX=0 NormalY=0 NormalZ=1 AngleXU=-1.5708 Radius=0.186667 StartAngle=0 EndAngle=1.5708
FEATURE [App::DocumentObjectGroup] Group002  label="Shape2D"
  Group = -> [Shape2DView010,Shape2DView006,Shape2DView004,Shape2DView005,Shape2DView008,Shape2DView002,Shape2DView007,Shape2DView009,Shape2DView003,Shape2DView012,Shape2DView011]
FEATURE [App::DocumentObjectGroup] Group003  label="Solids"
  Group = -> [test009,test010,Chamfer,Chamfer001,Chamfer002,Chamfer003,Chamfer004,Chamfer005,Chamfer007,Chamfer006,Chamfer008]
